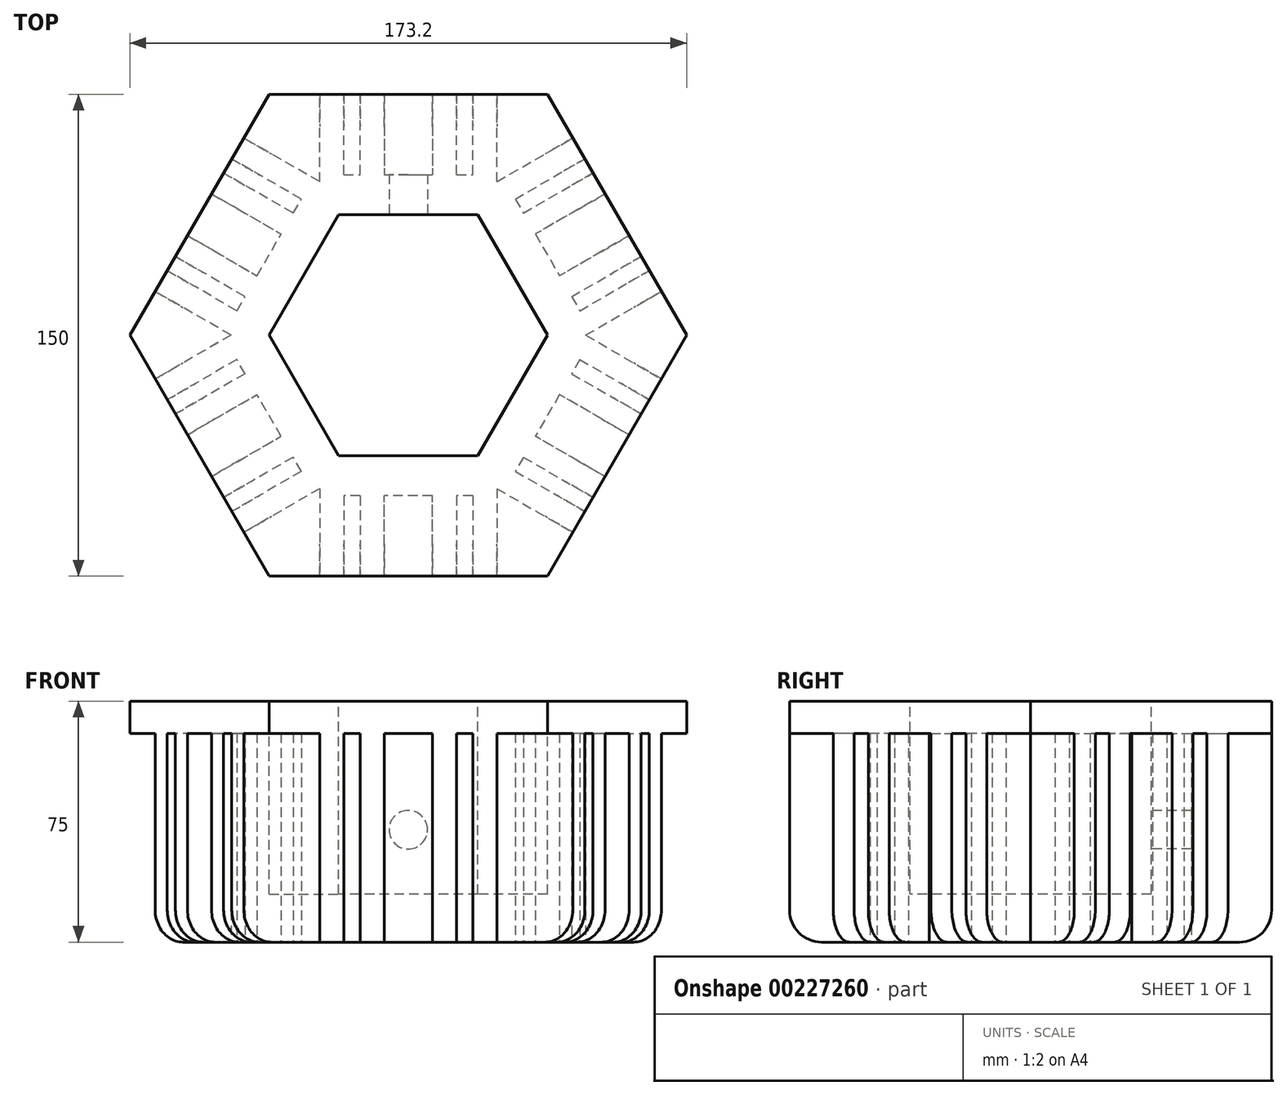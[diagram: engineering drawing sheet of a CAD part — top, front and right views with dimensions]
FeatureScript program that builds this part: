
annotation { "Feature Type Name" : "Feature", "Feature Type Description" : "" }
export const myFeature = defineFeature(function(context is Context, id is Id, definition is map)
    precondition{}
    {
        {
            var Q0;
            Q0=qCreatedBy(makeId("Top.planeOp"),FACE);
            var sketch = newSketch(context, id + "F0", { "sketchPlane" : qUnion([Q0])});
            skCircle(sketch, "E0.cCircle", {"center": v(0, 0) * mm, "radius": 75 * mm, "construction": true});
            skLineSegment(sketch, "E0.0", {"start": v(43.3, -75) * mm, "end": v(-43.3, -75) * mm});
            skLineSegment(sketch, "E0.1", {"start": v(-43.3, -75) * mm, "end": v(-86.6, 0) * mm});
            skLineSegment(sketch, "E0.2", {"start": v(-86.6, 0) * mm, "end": v(-43.3, 75) * mm});
            skLineSegment(sketch, "E0.3", {"start": v(-43.3, 75) * mm, "end": v(43.3, 75) * mm});
            skLineSegment(sketch, "E0.4", {"start": v(43.3, 75) * mm, "end": v(86.6, 0) * mm});
            skLineSegment(sketch, "E0.5", {"start": v(86.6, 0) * mm, "end": v(43.3, -75) * mm});
            skPoint(sketch, "E0.0.midPoint", {"position": v(0, -75) * mm});
            skCircle(sketch, "E1.cCircle", {"center": v(0, 0) * mm, "radius": 37.5 * mm, "construction": true});
            skLineSegment(sketch, "E1.0", {"start": v(21.65, -37.5) * mm, "end": v(-21.65, -37.5) * mm});
            skLineSegment(sketch, "E1.1", {"start": v(-21.65, -37.5) * mm, "end": v(-43.3, 0) * mm});
            skLineSegment(sketch, "E1.2", {"start": v(-43.3, 0) * mm, "end": v(-21.65, 37.5) * mm});
            skLineSegment(sketch, "E1.3", {"start": v(-21.65, 37.5) * mm, "end": v(21.65, 37.5) * mm});
            skLineSegment(sketch, "E1.4", {"start": v(21.65, 37.5) * mm, "end": v(43.3, 0) * mm});
            skLineSegment(sketch, "E1.5", {"start": v(43.3, 0) * mm, "end": v(21.65, -37.5) * mm});
            skPoint(sketch, "E1.0.midPoint", {"position": v(0, -37.5) * mm});
            skLineSegment(sketch, "E2", {"start": v(-15, 37.5) * mm, "end": v(-15, 75) * mm});
            skLineSegment(sketch, "E3", {"start": v(-20.08, 37.5) * mm, "end": v(-20.08, 75) * mm});
            skLineSegment(sketch, "E4", {"start": v(-27.58, 37.5) * mm, "end": v(-27.58, 75) * mm});
            skLineSegment(sketch, "E5", {"start": v(-7.5, 75) * mm, "end": v(-7.5, 37.5) * mm});
            skLineSegment(sketch, "E6.MirrorCS", {"start": v(7.5, 75) * mm, "end": v(7.5, 37.5) * mm});
            skLineSegment(sketch, "E7.MirrorCS", {"start": v(15, 37.5) * mm, "end": v(15, 75) * mm});
            skLineSegment(sketch, "E8.MirrorCS", {"start": v(20.08, 37.5) * mm, "end": v(20.08, 75) * mm});
            skLineSegment(sketch, "E9.MirrorCS", {"start": v(27.58, 37.5) * mm, "end": v(27.58, 75) * mm});
            skLineSegment(sketch, "E10", {"start": v(-27.58, 50) * mm, "end": v(27.58, 50) * mm});
            skLineSegment(sketch, "E11.1.0", {"start": v(-42.52, 1.36) * mm, "end": v(-75, 20.11) * mm});
            skLineSegment(sketch, "E11.1.1", {"start": v(-46.27, -5.13) * mm, "end": v(-78.74, 13.62) * mm});
            skLineSegment(sketch, "E11.1.2", {"start": v(-39.98, 5.76) * mm, "end": v(-72.45, 24.5) * mm});
            skLineSegment(sketch, "E11.1.3", {"start": v(-68.7, 31) * mm, "end": v(-36.23, 12.25) * mm});
            skLineSegment(sketch, "E11.1.4", {"start": v(-61.2, 44) * mm, "end": v(-28.73, 25.25) * mm});
            skLineSegment(sketch, "E11.1.5", {"start": v(-24.98, 31.74) * mm, "end": v(-57.45, 50.5) * mm});
            skLineSegment(sketch, "E11.1.6", {"start": v(-22.44, 36.14) * mm, "end": v(-54.91, 54.89) * mm});
            skLineSegment(sketch, "E11.1.7", {"start": v(-18.69, 42.63) * mm, "end": v(-51.16, 61.38) * mm});
            skLineSegment(sketch, "E11.1.8", {"start": v(-57.1, 1.12) * mm, "end": v(-29.51, 48.88) * mm});
            skLineSegment(sketch, "E11.2.0", {"start": v(-22.44, -36.14) * mm, "end": v(-54.91, -54.89) * mm});
            skLineSegment(sketch, "E11.2.1", {"start": v(-18.69, -42.63) * mm, "end": v(-51.16, -61.38) * mm});
            skLineSegment(sketch, "E11.2.2", {"start": v(-24.98, -31.74) * mm, "end": v(-57.45, -50.5) * mm});
            skLineSegment(sketch, "E11.2.3", {"start": v(-61.2, -44) * mm, "end": v(-28.73, -25.25) * mm});
            skLineSegment(sketch, "E11.2.4", {"start": v(-68.7, -31) * mm, "end": v(-36.23, -12.25) * mm});
            skLineSegment(sketch, "E11.2.5", {"start": v(-39.98, -5.76) * mm, "end": v(-72.45, -24.5) * mm});
            skLineSegment(sketch, "E11.2.6", {"start": v(-42.52, -1.36) * mm, "end": v(-75, -20.11) * mm});
            skLineSegment(sketch, "E11.2.7", {"start": v(-46.27, 5.13) * mm, "end": v(-78.74, -13.62) * mm});
            skLineSegment(sketch, "E11.2.8", {"start": v(-29.51, -48.88) * mm, "end": v(-57.1, -1.12) * mm});
            skLineSegment(sketch, "E11.3.0", {"start": v(20.08, -37.5) * mm, "end": v(20.08, -75) * mm});
            skLineSegment(sketch, "E11.3.1", {"start": v(27.58, -37.5) * mm, "end": v(27.58, -75) * mm});
            skLineSegment(sketch, "E11.3.2", {"start": v(15, -37.5) * mm, "end": v(15, -75) * mm});
            skLineSegment(sketch, "E11.3.3", {"start": v(7.5, -75) * mm, "end": v(7.5, -37.5) * mm});
            skLineSegment(sketch, "E11.3.4", {"start": v(-7.5, -75) * mm, "end": v(-7.5, -37.5) * mm});
            skLineSegment(sketch, "E11.3.5", {"start": v(-15, -37.5) * mm, "end": v(-15, -75) * mm});
            skLineSegment(sketch, "E11.3.6", {"start": v(-20.08, -37.5) * mm, "end": v(-20.08, -75) * mm});
            skLineSegment(sketch, "E11.3.7", {"start": v(-27.58, -37.5) * mm, "end": v(-27.58, -75) * mm});
            skLineSegment(sketch, "E11.3.8", {"start": v(27.58, -50) * mm, "end": v(-27.58, -50) * mm});
            skLineSegment(sketch, "E11.4.0", {"start": v(42.52, -1.36) * mm, "end": v(75, -20.11) * mm});
            skLineSegment(sketch, "E11.4.1", {"start": v(46.27, 5.13) * mm, "end": v(78.74, -13.62) * mm});
            skLineSegment(sketch, "E11.4.2", {"start": v(39.98, -5.76) * mm, "end": v(72.45, -24.5) * mm});
            skLineSegment(sketch, "E11.4.3", {"start": v(68.7, -31) * mm, "end": v(36.23, -12.25) * mm});
            skLineSegment(sketch, "E11.4.4", {"start": v(61.2, -44) * mm, "end": v(28.73, -25.25) * mm});
            skLineSegment(sketch, "E11.4.5", {"start": v(24.98, -31.74) * mm, "end": v(57.45, -50.5) * mm});
            skLineSegment(sketch, "E11.4.6", {"start": v(22.44, -36.14) * mm, "end": v(54.91, -54.89) * mm});
            skLineSegment(sketch, "E11.4.7", {"start": v(18.69, -42.63) * mm, "end": v(51.16, -61.38) * mm});
            skLineSegment(sketch, "E11.4.8", {"start": v(57.1, -1.12) * mm, "end": v(29.51, -48.88) * mm});
            skLineSegment(sketch, "E11.5.0", {"start": v(22.44, 36.14) * mm, "end": v(54.91, 54.89) * mm});
            skLineSegment(sketch, "E11.5.1", {"start": v(18.69, 42.63) * mm, "end": v(51.16, 61.38) * mm});
            skLineSegment(sketch, "E11.5.2", {"start": v(24.98, 31.74) * mm, "end": v(57.45, 50.5) * mm});
            skLineSegment(sketch, "E11.5.3", {"start": v(61.2, 44) * mm, "end": v(28.73, 25.25) * mm});
            skLineSegment(sketch, "E11.5.4", {"start": v(68.7, 31) * mm, "end": v(36.23, 12.25) * mm});
            skLineSegment(sketch, "E11.5.5", {"start": v(39.98, 5.76) * mm, "end": v(72.45, 24.5) * mm});
            skLineSegment(sketch, "E11.5.6", {"start": v(42.52, 1.36) * mm, "end": v(75, 20.11) * mm});
            skLineSegment(sketch, "E11.5.7", {"start": v(46.27, -5.13) * mm, "end": v(78.74, 13.62) * mm});
            skLineSegment(sketch, "E11.5.8", {"start": v(29.51, 48.88) * mm, "end": v(57.1, 1.12) * mm});
            skSolve(sketch);
        }
        {
            var Q0;
            {var subQ0=sQuery(id+"F0.wireOp",EDGE,"E3");var subQ1=sQuery(id+"F0.wireOp",EDGE,"E0.3");var subQ2=makeQuery(id+"F0.imprint","INTERSECT",VERTEX,{"derivedFrom":[subQ1,subQ0]});Q0=makeQuery(id+"F0.imprint","IMPRINT",FACE,{"disambiguationData":[TD([[makeQuery(id+"F0.imprint","IMPRINT",EDGE,{"disambiguationData":[TD([[subQ2,1.0]])],"derivedFrom":subQ1}),-1.0]])]});}
            var Q1;
            {var subQ0=sQuery(id+"F0.wireOp",EDGE,"E2");var subQ1=sQuery(id+"F0.wireOp",EDGE,"E0.3");var subQ2=makeQuery(id+"F0.imprint","INTERSECT",VERTEX,{"derivedFrom":[subQ1,subQ0]});Q1=makeQuery(id+"F0.imprint","IMPRINT",FACE,{"disambiguationData":[TD([[makeQuery(id+"F0.imprint","IMPRINT",EDGE,{"disambiguationData":[TD([[subQ2,1.0]])],"derivedFrom":subQ1}),-1.0]])]});}
            var Q2;
            {var subQ0=sQuery(id+"F0.wireOp",EDGE,"E2");var subQ1=sQuery(id+"F0.wireOp",EDGE,"E0.3");var subQ2=makeQuery(id+"F0.imprint","INTERSECT",VERTEX,{"derivedFrom":[subQ1,subQ0]});Q2=makeQuery(id+"F0.imprint","IMPRINT",FACE,{"disambiguationData":[TD([[makeQuery(id+"F0.imprint","IMPRINT",EDGE,{"disambiguationData":[TD([[subQ2,-1.0]])],"derivedFrom":subQ1}),-1.0]])]});}
            var Q3;
            {var subQ0=sQuery(id+"F0.wireOp",EDGE,"E5");var subQ1=sQuery(id+"F0.wireOp",EDGE,"E0.3");var subQ2=makeQuery(id+"F0.imprint","INTERSECT",VERTEX,{"derivedFrom":[subQ1,subQ0]});Q3=makeQuery(id+"F0.imprint","IMPRINT",FACE,{"disambiguationData":[TD([[makeQuery(id+"F0.imprint","IMPRINT",EDGE,{"disambiguationData":[TD([[subQ2,-1.0]])],"derivedFrom":subQ1}),-1.0]])]});}
            var Q4;
            {var subQ0=sQuery(id+"F0.wireOp",EDGE,"E6.MirrorCS");var subQ1=sQuery(id+"F0.wireOp",EDGE,"E0.3");var subQ2=makeQuery(id+"F0.imprint","INTERSECT",VERTEX,{"derivedFrom":[subQ1,subQ0]});Q4=makeQuery(id+"F0.imprint","IMPRINT",FACE,{"disambiguationData":[TD([[makeQuery(id+"F0.imprint","IMPRINT",EDGE,{"disambiguationData":[TD([[subQ2,-1.0]])],"derivedFrom":subQ1}),-1.0]])]});}
            var Q5;
            {var subQ0=sQuery(id+"F0.wireOp",EDGE,"E7.MirrorCS");var subQ1=sQuery(id+"F0.wireOp",EDGE,"E0.3");var subQ2=makeQuery(id+"F0.imprint","INTERSECT",VERTEX,{"derivedFrom":[subQ1,subQ0]});Q5=makeQuery(id+"F0.imprint","IMPRINT",FACE,{"disambiguationData":[TD([[makeQuery(id+"F0.imprint","IMPRINT",EDGE,{"disambiguationData":[TD([[subQ2,-1.0]])],"derivedFrom":subQ1}),-1.0]])]});}
            var Q6;
            {var subQ0=sQuery(id+"F0.wireOp",EDGE,"E8.MirrorCS");var subQ1=sQuery(id+"F0.wireOp",EDGE,"E0.3");var subQ2=makeQuery(id+"F0.imprint","INTERSECT",VERTEX,{"derivedFrom":[subQ1,subQ0]});Q6=makeQuery(id+"F0.imprint","IMPRINT",FACE,{"disambiguationData":[TD([[makeQuery(id+"F0.imprint","IMPRINT",EDGE,{"disambiguationData":[TD([[subQ2,-1.0]])],"derivedFrom":subQ1}),-1.0]])]});}
            var Q7;
            {var subQ1=sQuery(id+"F0.wireOp",EDGE,"E0.3");var subQ6=sQuery(id+"F0.wireOp",EDGE,"E0.4");var subQ7=makeQuery(id+"F0.imprint","INTERSECT",VERTEX,{"derivedFrom":[subQ1,subQ6]});Q7=makeQuery(id+"F0.imprint","IMPRINT",FACE,{"disambiguationData":[TD([[makeQuery(id+"F0.imprint","IMPRINT",EDGE,{"disambiguationData":[TD([[subQ7,1.0]])],"derivedFrom":subQ1}),-1.0]])]});}
            var Q8;
            {var subQ0=sQuery(id+"F0.wireOp",EDGE,"E11.5.0");var subQ1=sQuery(id+"F0.wireOp",EDGE,"E0.4");var subQ2=makeQuery(id+"F0.imprint","INTERSECT",VERTEX,{"derivedFrom":[subQ1,subQ0]});Q8=makeQuery(id+"F0.imprint","IMPRINT",FACE,{"disambiguationData":[TD([[makeQuery(id+"F0.imprint","IMPRINT",EDGE,{"disambiguationData":[TD([[subQ2,1.0]])],"derivedFrom":subQ1}),-1.0]])]});}
            var Q9;
            {var subQ0=sQuery(id+"F0.wireOp",EDGE,"E11.1.7");var subQ1=sQuery(id+"F0.wireOp",EDGE,"E3");var subQ2=makeQuery(id+"F0.imprint","INTERSECT",VERTEX,{"derivedFrom":[subQ1,subQ0]});Q9=makeQuery(id+"F0.imprint","IMPRINT",FACE,{"disambiguationData":[TD([[makeQuery(id+"F0.imprint","IMPRINT",EDGE,{"disambiguationData":[TD([[subQ2,-1.0]])],"derivedFrom":subQ1}),1.0]])]});}
            var Q10;
            {var subQ6=sQuery(id+"F0.wireOp",EDGE,"E1.3");var subQ9=sQuery(id+"F0.wireOp",EDGE,"E1.2");var subQ10=makeQuery(id+"F0.imprint","INTERSECT",VERTEX,{"derivedFrom":[subQ9,subQ6]});Q10=makeQuery(id+"F0.imprint","IMPRINT",FACE,{"disambiguationData":[TD([[makeQuery(id+"F0.imprint","IMPRINT",EDGE,{"disambiguationData":[TD([[subQ10,1.0]])],"derivedFrom":subQ9}),1.0]])]});}
            var Q11;
            {var subQ4=sQuery(id+"F0.wireOp",EDGE,"E1.3");var subQ6=sQuery(id+"F0.wireOp",EDGE,"E2");var subQ7=makeQuery(id+"F0.imprint","INTERSECT",VERTEX,{"derivedFrom":[subQ4,subQ6]});Q11=makeQuery(id+"F0.imprint","IMPRINT",FACE,{"disambiguationData":[TD([[makeQuery(id+"F0.imprint","IMPRINT",EDGE,{"disambiguationData":[TD([[subQ7,1.0]])],"derivedFrom":subQ4}),1.0]])]});}
            var Q12;
            {var subQ0=sQuery(id+"F0.wireOp",EDGE,"E2");var subQ1=sQuery(id+"F0.wireOp",EDGE,"E1.3");var subQ2=makeQuery(id+"F0.imprint","INTERSECT",VERTEX,{"derivedFrom":[subQ1,subQ0]});Q12=makeQuery(id+"F0.imprint","IMPRINT",FACE,{"disambiguationData":[TD([[makeQuery(id+"F0.imprint","IMPRINT",EDGE,{"disambiguationData":[TD([[subQ2,-1.0]])],"derivedFrom":subQ1}),1.0]])]});}
            var Q13;
            {var subQ0=sQuery(id+"F0.wireOp",EDGE,"E5");var subQ1=sQuery(id+"F0.wireOp",EDGE,"E1.3");var subQ2=makeQuery(id+"F0.imprint","INTERSECT",VERTEX,{"derivedFrom":[subQ1,subQ0]});Q13=makeQuery(id+"F0.imprint","IMPRINT",FACE,{"disambiguationData":[TD([[makeQuery(id+"F0.imprint","IMPRINT",EDGE,{"disambiguationData":[TD([[subQ2,-1.0]])],"derivedFrom":subQ1}),1.0]])]});}
            var Q14;
            {var subQ0=sQuery(id+"F0.wireOp",EDGE,"E6.MirrorCS");var subQ1=sQuery(id+"F0.wireOp",EDGE,"E1.3");var subQ2=makeQuery(id+"F0.imprint","INTERSECT",VERTEX,{"derivedFrom":[subQ1,subQ0]});Q14=makeQuery(id+"F0.imprint","IMPRINT",FACE,{"disambiguationData":[TD([[makeQuery(id+"F0.imprint","IMPRINT",EDGE,{"disambiguationData":[TD([[subQ2,-1.0]])],"derivedFrom":subQ1}),1.0]])]});}
            var Q15;
            {var subQ4=sQuery(id+"F0.wireOp",EDGE,"E1.3");var subQ6=sQuery(id+"F0.wireOp",EDGE,"E7.MirrorCS");var subQ8=makeQuery(id+"F0.imprint","INTERSECT",VERTEX,{"derivedFrom":[subQ4,subQ6]});Q15=makeQuery(id+"F0.imprint","IMPRINT",FACE,{"disambiguationData":[TD([[makeQuery(id+"F0.imprint","IMPRINT",EDGE,{"disambiguationData":[TD([[subQ8,-1.0]])],"derivedFrom":subQ4}),1.0]])]});}
            var Q16;
            {var subQ5=sQuery(id+"F0.wireOp",EDGE,"E1.4");var subQ6=sQuery(id+"F0.wireOp",EDGE,"E1.3");var subQ7=makeQuery(id+"F0.imprint","INTERSECT",VERTEX,{"derivedFrom":[subQ6,subQ5]});Q16=makeQuery(id+"F0.imprint","IMPRINT",FACE,{"disambiguationData":[TD([[makeQuery(id+"F0.imprint","IMPRINT",EDGE,{"disambiguationData":[TD([[subQ7,1.0]])],"derivedFrom":subQ6}),1.0]])]});}
            var Q17;
            {var subQ0=sQuery(id+"F0.wireOp",EDGE,"E11.5.1");var subQ1=sQuery(id+"F0.wireOp",EDGE,"E8.MirrorCS");var subQ2=makeQuery(id+"F0.imprint","INTERSECT",VERTEX,{"derivedFrom":[subQ1,subQ0]});Q17=makeQuery(id+"F0.imprint","IMPRINT",FACE,{"disambiguationData":[TD([[makeQuery(id+"F0.imprint","IMPRINT",EDGE,{"disambiguationData":[TD([[subQ2,-1.0]])],"derivedFrom":subQ1}),-1.0]])]});}
            var Q18;
            {var subQ0=sQuery(id+"F0.wireOp",EDGE,"E11.5.0");var subQ1=sQuery(id+"F0.wireOp",EDGE,"E9.MirrorCS");var subQ2=makeQuery(id+"F0.imprint","INTERSECT",VERTEX,{"derivedFrom":[subQ1,subQ0]});Q18=makeQuery(id+"F0.imprint","IMPRINT",FACE,{"disambiguationData":[TD([[makeQuery(id+"F0.imprint","IMPRINT",EDGE,{"disambiguationData":[TD([[subQ2,-1.0]])],"derivedFrom":subQ1}),-1.0]])]});}
            var Q19;
            {var subQ1=sQuery(id+"F0.wireOp",EDGE,"E1.4");var subQ5=sQuery(id+"F0.wireOp",EDGE,"E11.5.0");var subQ8=makeQuery(id+"F0.imprint","INTERSECT",VERTEX,{"derivedFrom":[subQ1,subQ5]});Q19=makeQuery(id+"F0.imprint","IMPRINT",FACE,{"disambiguationData":[TD([[makeQuery(id+"F0.imprint","IMPRINT",EDGE,{"disambiguationData":[TD([[subQ8,-1.0]])],"derivedFrom":subQ1}),1.0]])]});}
            var Q20;
            {var subQ0=sQuery(id+"F0.wireOp",EDGE,"E11.5.0");var subQ1=sQuery(id+"F0.wireOp",EDGE,"E0.4");var subQ2=makeQuery(id+"F0.imprint","INTERSECT",VERTEX,{"derivedFrom":[subQ1,subQ0]});Q20=makeQuery(id+"F0.imprint","IMPRINT",FACE,{"disambiguationData":[TD([[makeQuery(id+"F0.imprint","IMPRINT",EDGE,{"disambiguationData":[TD([[subQ2,-1.0]])],"derivedFrom":subQ1}),-1.0]])]});}
            var Q21;
            {var subQ0=sQuery(id+"F0.wireOp",EDGE,"E11.5.2");var subQ1=sQuery(id+"F0.wireOp",EDGE,"E1.4");var subQ2=makeQuery(id+"F0.imprint","INTERSECT",VERTEX,{"derivedFrom":[subQ1,subQ0]});Q21=makeQuery(id+"F0.imprint","IMPRINT",FACE,{"disambiguationData":[TD([[makeQuery(id+"F0.imprint","IMPRINT",EDGE,{"disambiguationData":[TD([[subQ2,-1.0]])],"derivedFrom":subQ1}),1.0]])]});}
            var Q22;
            {var subQ0=sQuery(id+"F0.wireOp",EDGE,"E11.5.2");var subQ1=sQuery(id+"F0.wireOp",EDGE,"E0.4");var subQ2=makeQuery(id+"F0.imprint","INTERSECT",VERTEX,{"derivedFrom":[subQ1,subQ0]});Q22=makeQuery(id+"F0.imprint","IMPRINT",FACE,{"disambiguationData":[TD([[makeQuery(id+"F0.imprint","IMPRINT",EDGE,{"disambiguationData":[TD([[subQ2,-1.0]])],"derivedFrom":subQ1}),-1.0]])]});}
            var Q23;
            {var subQ0=sQuery(id+"F0.wireOp",EDGE,"E11.5.3");var subQ1=sQuery(id+"F0.wireOp",EDGE,"E1.4");var subQ2=makeQuery(id+"F0.imprint","INTERSECT",VERTEX,{"derivedFrom":[subQ1,subQ0]});Q23=makeQuery(id+"F0.imprint","IMPRINT",FACE,{"disambiguationData":[TD([[makeQuery(id+"F0.imprint","IMPRINT",EDGE,{"disambiguationData":[TD([[subQ2,-1.0]])],"derivedFrom":subQ1}),1.0]])]});}
            var Q24;
            {var subQ0=sQuery(id+"F0.wireOp",EDGE,"E11.5.3");var subQ1=sQuery(id+"F0.wireOp",EDGE,"E0.4");var subQ2=makeQuery(id+"F0.imprint","INTERSECT",VERTEX,{"derivedFrom":[subQ1,subQ0]});Q24=makeQuery(id+"F0.imprint","IMPRINT",FACE,{"disambiguationData":[TD([[makeQuery(id+"F0.imprint","IMPRINT",EDGE,{"disambiguationData":[TD([[subQ2,-1.0]])],"derivedFrom":subQ1}),-1.0]])]});}
            var Q25;
            {var subQ0=sQuery(id+"F0.wireOp",EDGE,"E11.5.4");var subQ1=sQuery(id+"F0.wireOp",EDGE,"E1.4");var subQ2=makeQuery(id+"F0.imprint","INTERSECT",VERTEX,{"derivedFrom":[subQ1,subQ0]});Q25=makeQuery(id+"F0.imprint","IMPRINT",FACE,{"disambiguationData":[TD([[makeQuery(id+"F0.imprint","IMPRINT",EDGE,{"disambiguationData":[TD([[subQ2,-1.0]])],"derivedFrom":subQ1}),1.0]])]});}
            var Q26;
            {var subQ0=sQuery(id+"F0.wireOp",EDGE,"E11.5.4");var subQ1=sQuery(id+"F0.wireOp",EDGE,"E0.4");var subQ2=makeQuery(id+"F0.imprint","INTERSECT",VERTEX,{"derivedFrom":[subQ1,subQ0]});Q26=makeQuery(id+"F0.imprint","IMPRINT",FACE,{"disambiguationData":[TD([[makeQuery(id+"F0.imprint","IMPRINT",EDGE,{"disambiguationData":[TD([[subQ2,-1.0]])],"derivedFrom":subQ1}),-1.0]])]});}
            var Q27;
            {var subQ4=sQuery(id+"F0.wireOp",EDGE,"E1.4");var subQ6=sQuery(id+"F0.wireOp",EDGE,"E11.5.5");var subQ8=makeQuery(id+"F0.imprint","INTERSECT",VERTEX,{"derivedFrom":[subQ4,subQ6]});Q27=makeQuery(id+"F0.imprint","IMPRINT",FACE,{"disambiguationData":[TD([[makeQuery(id+"F0.imprint","IMPRINT",EDGE,{"disambiguationData":[TD([[subQ8,-1.0]])],"derivedFrom":subQ4}),1.0]])]});}
            var Q28;
            {var subQ6=sQuery(id+"F0.wireOp",EDGE,"E1.5");var subQ9=sQuery(id+"F0.wireOp",EDGE,"E1.4");var subQ10=makeQuery(id+"F0.imprint","INTERSECT",VERTEX,{"derivedFrom":[subQ9,subQ6]});Q28=makeQuery(id+"F0.imprint","IMPRINT",FACE,{"disambiguationData":[TD([[makeQuery(id+"F0.imprint","IMPRINT",EDGE,{"disambiguationData":[TD([[subQ10,1.0]])],"derivedFrom":subQ9}),1.0]])]});}
            var Q29;
            {var subQ0=sQuery(id+"F0.wireOp",EDGE,"E11.5.6");var subQ1=sQuery(id+"F0.wireOp",EDGE,"E11.4.1");var subQ2=makeQuery(id+"F0.imprint","INTERSECT",VERTEX,{"derivedFrom":[subQ1,subQ0]});Q29=makeQuery(id+"F0.imprint","IMPRINT",FACE,{"disambiguationData":[TD([[makeQuery(id+"F0.imprint","IMPRINT",EDGE,{"disambiguationData":[TD([[subQ2,-1.0]])],"derivedFrom":subQ1}),1.0]])]});}
            var Q30;
            {var subQ0=sQuery(id+"F0.wireOp",EDGE,"E11.5.5");var subQ1=sQuery(id+"F0.wireOp",EDGE,"E0.4");var subQ2=makeQuery(id+"F0.imprint","INTERSECT",VERTEX,{"derivedFrom":[subQ1,subQ0]});Q30=makeQuery(id+"F0.imprint","IMPRINT",FACE,{"disambiguationData":[TD([[makeQuery(id+"F0.imprint","IMPRINT",EDGE,{"disambiguationData":[TD([[subQ2,-1.0]])],"derivedFrom":subQ1}),-1.0]])]});}
            var Q31;
            {var subQ0=sQuery(id+"F0.wireOp",EDGE,"E11.5.6");var subQ1=sQuery(id+"F0.wireOp",EDGE,"E0.4");var subQ2=makeQuery(id+"F0.imprint","INTERSECT",VERTEX,{"derivedFrom":[subQ1,subQ0]});Q31=makeQuery(id+"F0.imprint","IMPRINT",FACE,{"disambiguationData":[TD([[makeQuery(id+"F0.imprint","IMPRINT",EDGE,{"disambiguationData":[TD([[subQ2,-1.0]])],"derivedFrom":subQ1}),-1.0]])]});}
            var Q32;
            {var subQ1=sQuery(id+"F0.wireOp",EDGE,"E0.5");var subQ6=sQuery(id+"F0.wireOp",EDGE,"E0.4");var subQ7=makeQuery(id+"F0.imprint","INTERSECT",VERTEX,{"derivedFrom":[subQ6,subQ1]});Q32=makeQuery(id+"F0.imprint","IMPRINT",FACE,{"disambiguationData":[TD([[makeQuery(id+"F0.imprint","IMPRINT",EDGE,{"disambiguationData":[TD([[subQ7,1.0]])],"derivedFrom":subQ6}),-1.0]])]});}
            var Q33;
            {var subQ0=sQuery(id+"F0.wireOp",EDGE,"E11.4.0");var subQ1=sQuery(id+"F0.wireOp",EDGE,"E0.5");var subQ2=makeQuery(id+"F0.imprint","INTERSECT",VERTEX,{"derivedFrom":[subQ1,subQ0]});Q33=makeQuery(id+"F0.imprint","IMPRINT",FACE,{"disambiguationData":[TD([[makeQuery(id+"F0.imprint","IMPRINT",EDGE,{"disambiguationData":[TD([[subQ2,1.0]])],"derivedFrom":subQ1}),-1.0]])]});}
            var Q34;
            {var subQ0=sQuery(id+"F0.wireOp",EDGE,"E11.5.7");var subQ1=sQuery(id+"F0.wireOp",EDGE,"E11.4.0");var subQ2=makeQuery(id+"F0.imprint","INTERSECT",VERTEX,{"derivedFrom":[subQ1,subQ0]});Q34=makeQuery(id+"F0.imprint","IMPRINT",FACE,{"disambiguationData":[TD([[makeQuery(id+"F0.imprint","IMPRINT",EDGE,{"disambiguationData":[TD([[subQ2,-1.0]])],"derivedFrom":subQ1}),1.0]])]});}
            var Q35;
            {var subQ1=sQuery(id+"F0.wireOp",EDGE,"E1.5");var subQ5=sQuery(id+"F0.wireOp",EDGE,"E11.4.0");var subQ6=makeQuery(id+"F0.imprint","INTERSECT",VERTEX,{"derivedFrom":[subQ1,subQ5]});Q35=makeQuery(id+"F0.imprint","IMPRINT",FACE,{"disambiguationData":[TD([[makeQuery(id+"F0.imprint","IMPRINT",EDGE,{"disambiguationData":[TD([[subQ6,-1.0]])],"derivedFrom":subQ1}),1.0]])]});}
            var Q36;
            {var subQ0=sQuery(id+"F0.wireOp",EDGE,"E11.4.0");var subQ1=sQuery(id+"F0.wireOp",EDGE,"E0.5");var subQ2=makeQuery(id+"F0.imprint","INTERSECT",VERTEX,{"derivedFrom":[subQ1,subQ0]});Q36=makeQuery(id+"F0.imprint","IMPRINT",FACE,{"disambiguationData":[TD([[makeQuery(id+"F0.imprint","IMPRINT",EDGE,{"disambiguationData":[TD([[subQ2,-1.0]])],"derivedFrom":subQ1}),-1.0]])]});}
            var Q37;
            {var subQ0=sQuery(id+"F0.wireOp",EDGE,"E11.4.2");var subQ1=sQuery(id+"F0.wireOp",EDGE,"E0.5");var subQ2=makeQuery(id+"F0.imprint","INTERSECT",VERTEX,{"derivedFrom":[subQ1,subQ0]});Q37=makeQuery(id+"F0.imprint","IMPRINT",FACE,{"disambiguationData":[TD([[makeQuery(id+"F0.imprint","IMPRINT",EDGE,{"disambiguationData":[TD([[subQ2,-1.0]])],"derivedFrom":subQ1}),-1.0]])]});}
            var Q38;
            {var subQ0=sQuery(id+"F0.wireOp",EDGE,"E11.4.2");var subQ1=sQuery(id+"F0.wireOp",EDGE,"E1.5");var subQ2=makeQuery(id+"F0.imprint","INTERSECT",VERTEX,{"derivedFrom":[subQ1,subQ0]});Q38=makeQuery(id+"F0.imprint","IMPRINT",FACE,{"disambiguationData":[TD([[makeQuery(id+"F0.imprint","IMPRINT",EDGE,{"disambiguationData":[TD([[subQ2,-1.0]])],"derivedFrom":subQ1}),1.0]])]});}
            var Q39;
            {var subQ0=sQuery(id+"F0.wireOp",EDGE,"E11.4.3");var subQ1=sQuery(id+"F0.wireOp",EDGE,"E1.5");var subQ2=makeQuery(id+"F0.imprint","INTERSECT",VERTEX,{"derivedFrom":[subQ1,subQ0]});Q39=makeQuery(id+"F0.imprint","IMPRINT",FACE,{"disambiguationData":[TD([[makeQuery(id+"F0.imprint","IMPRINT",EDGE,{"disambiguationData":[TD([[subQ2,-1.0]])],"derivedFrom":subQ1}),1.0]])]});}
            var Q40;
            {var subQ0=sQuery(id+"F0.wireOp",EDGE,"E11.4.3");var subQ1=sQuery(id+"F0.wireOp",EDGE,"E0.5");var subQ2=makeQuery(id+"F0.imprint","INTERSECT",VERTEX,{"derivedFrom":[subQ1,subQ0]});Q40=makeQuery(id+"F0.imprint","IMPRINT",FACE,{"disambiguationData":[TD([[makeQuery(id+"F0.imprint","IMPRINT",EDGE,{"disambiguationData":[TD([[subQ2,-1.0]])],"derivedFrom":subQ1}),-1.0]])]});}
            var Q41;
            {var subQ0=sQuery(id+"F0.wireOp",EDGE,"E11.4.4");var subQ1=sQuery(id+"F0.wireOp",EDGE,"E1.5");var subQ2=makeQuery(id+"F0.imprint","INTERSECT",VERTEX,{"derivedFrom":[subQ1,subQ0]});Q41=makeQuery(id+"F0.imprint","IMPRINT",FACE,{"disambiguationData":[TD([[makeQuery(id+"F0.imprint","IMPRINT",EDGE,{"disambiguationData":[TD([[subQ2,-1.0]])],"derivedFrom":subQ1}),1.0]])]});}
            var Q42;
            {var subQ0=sQuery(id+"F0.wireOp",EDGE,"E11.4.4");var subQ1=sQuery(id+"F0.wireOp",EDGE,"E0.5");var subQ2=makeQuery(id+"F0.imprint","INTERSECT",VERTEX,{"derivedFrom":[subQ1,subQ0]});Q42=makeQuery(id+"F0.imprint","IMPRINT",FACE,{"disambiguationData":[TD([[makeQuery(id+"F0.imprint","IMPRINT",EDGE,{"disambiguationData":[TD([[subQ2,-1.0]])],"derivedFrom":subQ1}),-1.0]])]});}
            var Q43;
            {var subQ1=sQuery(id+"F0.wireOp",EDGE,"E1.5");var subQ6=sQuery(id+"F0.wireOp",EDGE,"E11.4.5");var subQ7=makeQuery(id+"F0.imprint","INTERSECT",VERTEX,{"derivedFrom":[subQ1,subQ6]});Q43=makeQuery(id+"F0.imprint","IMPRINT",FACE,{"disambiguationData":[TD([[makeQuery(id+"F0.imprint","IMPRINT",EDGE,{"disambiguationData":[TD([[subQ7,-1.0]])],"derivedFrom":subQ1}),1.0]])]});}
            var Q44;
            {var subQ0=sQuery(id+"F0.wireOp",EDGE,"E11.4.5");var subQ1=sQuery(id+"F0.wireOp",EDGE,"E0.5");var subQ2=makeQuery(id+"F0.imprint","INTERSECT",VERTEX,{"derivedFrom":[subQ1,subQ0]});Q44=makeQuery(id+"F0.imprint","IMPRINT",FACE,{"disambiguationData":[TD([[makeQuery(id+"F0.imprint","IMPRINT",EDGE,{"disambiguationData":[TD([[subQ2,-1.0]])],"derivedFrom":subQ1}),-1.0]])]});}
            var Q45;
            {var subQ0=sQuery(id+"F0.wireOp",EDGE,"E11.4.6");var subQ1=sQuery(id+"F0.wireOp",EDGE,"E0.5");var subQ2=makeQuery(id+"F0.imprint","INTERSECT",VERTEX,{"derivedFrom":[subQ1,subQ0]});Q45=makeQuery(id+"F0.imprint","IMPRINT",FACE,{"disambiguationData":[TD([[makeQuery(id+"F0.imprint","IMPRINT",EDGE,{"disambiguationData":[TD([[subQ2,-1.0]])],"derivedFrom":subQ1}),-1.0]])]});}
            var Q46;
            {var subQ6=sQuery(id+"F0.wireOp",EDGE,"E1.0");var subQ9=sQuery(id+"F0.wireOp",EDGE,"E1.5");var subQ10=makeQuery(id+"F0.imprint","INTERSECT",VERTEX,{"derivedFrom":[subQ6,subQ9]});Q46=makeQuery(id+"F0.imprint","IMPRINT",FACE,{"disambiguationData":[TD([[makeQuery(id+"F0.imprint","IMPRINT",EDGE,{"disambiguationData":[TD([[subQ10,-1.0]])],"derivedFrom":subQ6}),1.0]])]});}
            var Q47;
            {var subQ0=sQuery(id+"F0.wireOp",EDGE,"E11.4.6");var subQ1=sQuery(id+"F0.wireOp",EDGE,"E11.3.1");var subQ2=makeQuery(id+"F0.imprint","INTERSECT",VERTEX,{"derivedFrom":[subQ1,subQ0]});Q47=makeQuery(id+"F0.imprint","IMPRINT",FACE,{"disambiguationData":[TD([[makeQuery(id+"F0.imprint","IMPRINT",EDGE,{"disambiguationData":[TD([[subQ2,-1.0]])],"derivedFrom":subQ1}),1.0]])]});}
            var Q48;
            {var subQ1=sQuery(id+"F0.wireOp",EDGE,"E0.0");var subQ6=sQuery(id+"F0.wireOp",EDGE,"E0.5");var subQ7=makeQuery(id+"F0.imprint","INTERSECT",VERTEX,{"derivedFrom":[subQ1,subQ6]});Q48=makeQuery(id+"F0.imprint","IMPRINT",FACE,{"disambiguationData":[TD([[makeQuery(id+"F0.imprint","IMPRINT",EDGE,{"disambiguationData":[TD([[subQ7,-1.0]])],"derivedFrom":subQ1}),-1.0]])]});}
            var Q49;
            {var subQ0=sQuery(id+"F0.wireOp",EDGE,"E11.3.0");var subQ1=sQuery(id+"F0.wireOp",EDGE,"E0.0");var subQ2=makeQuery(id+"F0.imprint","INTERSECT",VERTEX,{"derivedFrom":[subQ1,subQ0]});Q49=makeQuery(id+"F0.imprint","IMPRINT",FACE,{"disambiguationData":[TD([[makeQuery(id+"F0.imprint","IMPRINT",EDGE,{"disambiguationData":[TD([[subQ2,1.0]])],"derivedFrom":subQ1}),-1.0]])]});}
            var Q50;
            {var subQ0=sQuery(id+"F0.wireOp",EDGE,"E11.4.7");var subQ1=sQuery(id+"F0.wireOp",EDGE,"E11.3.0");var subQ2=makeQuery(id+"F0.imprint","INTERSECT",VERTEX,{"derivedFrom":[subQ1,subQ0]});Q50=makeQuery(id+"F0.imprint","IMPRINT",FACE,{"disambiguationData":[TD([[makeQuery(id+"F0.imprint","IMPRINT",EDGE,{"disambiguationData":[TD([[subQ2,-1.0]])],"derivedFrom":subQ1}),1.0]])]});}
            var Q51;
            {var subQ1=sQuery(id+"F0.wireOp",EDGE,"E1.0");var subQ5=sQuery(id+"F0.wireOp",EDGE,"E11.3.0");var subQ8=makeQuery(id+"F0.imprint","INTERSECT",VERTEX,{"derivedFrom":[subQ1,subQ5]});Q51=makeQuery(id+"F0.imprint","IMPRINT",FACE,{"disambiguationData":[TD([[makeQuery(id+"F0.imprint","IMPRINT",EDGE,{"disambiguationData":[TD([[subQ8,-1.0]])],"derivedFrom":subQ1}),1.0]])]});}
            var Q52;
            {var subQ0=sQuery(id+"F0.wireOp",EDGE,"E11.3.0");var subQ1=sQuery(id+"F0.wireOp",EDGE,"E0.0");var subQ2=makeQuery(id+"F0.imprint","INTERSECT",VERTEX,{"derivedFrom":[subQ1,subQ0]});Q52=makeQuery(id+"F0.imprint","IMPRINT",FACE,{"disambiguationData":[TD([[makeQuery(id+"F0.imprint","IMPRINT",EDGE,{"disambiguationData":[TD([[subQ2,-1.0]])],"derivedFrom":subQ1}),-1.0]])]});}
            var Q53;
            {var subQ0=sQuery(id+"F0.wireOp",EDGE,"E11.3.2");var subQ1=sQuery(id+"F0.wireOp",EDGE,"E0.0");var subQ2=makeQuery(id+"F0.imprint","INTERSECT",VERTEX,{"derivedFrom":[subQ1,subQ0]});Q53=makeQuery(id+"F0.imprint","IMPRINT",FACE,{"disambiguationData":[TD([[makeQuery(id+"F0.imprint","IMPRINT",EDGE,{"disambiguationData":[TD([[subQ2,-1.0]])],"derivedFrom":subQ1}),-1.0]])]});}
            var Q54;
            {var subQ0=sQuery(id+"F0.wireOp",EDGE,"E11.3.2");var subQ1=sQuery(id+"F0.wireOp",EDGE,"E1.0");var subQ2=makeQuery(id+"F0.imprint","INTERSECT",VERTEX,{"derivedFrom":[subQ1,subQ0]});Q54=makeQuery(id+"F0.imprint","IMPRINT",FACE,{"disambiguationData":[TD([[makeQuery(id+"F0.imprint","IMPRINT",EDGE,{"disambiguationData":[TD([[subQ2,-1.0]])],"derivedFrom":subQ1}),1.0]])]});}
            var Q55;
            {var subQ0=sQuery(id+"F0.wireOp",EDGE,"E11.3.3");var subQ1=sQuery(id+"F0.wireOp",EDGE,"E1.0");var subQ2=makeQuery(id+"F0.imprint","INTERSECT",VERTEX,{"derivedFrom":[subQ1,subQ0]});Q55=makeQuery(id+"F0.imprint","IMPRINT",FACE,{"disambiguationData":[TD([[makeQuery(id+"F0.imprint","IMPRINT",EDGE,{"disambiguationData":[TD([[subQ2,-1.0]])],"derivedFrom":subQ1}),1.0]])]});}
            var Q56;
            {var subQ0=sQuery(id+"F0.wireOp",EDGE,"E11.3.3");var subQ1=sQuery(id+"F0.wireOp",EDGE,"E0.0");var subQ2=makeQuery(id+"F0.imprint","INTERSECT",VERTEX,{"derivedFrom":[subQ1,subQ0]});Q56=makeQuery(id+"F0.imprint","IMPRINT",FACE,{"disambiguationData":[TD([[makeQuery(id+"F0.imprint","IMPRINT",EDGE,{"disambiguationData":[TD([[subQ2,-1.0]])],"derivedFrom":subQ1}),-1.0]])]});}
            var Q57;
            {var subQ0=sQuery(id+"F0.wireOp",EDGE,"E11.3.4");var subQ1=sQuery(id+"F0.wireOp",EDGE,"E0.0");var subQ2=makeQuery(id+"F0.imprint","INTERSECT",VERTEX,{"derivedFrom":[subQ1,subQ0]});Q57=makeQuery(id+"F0.imprint","IMPRINT",FACE,{"disambiguationData":[TD([[makeQuery(id+"F0.imprint","IMPRINT",EDGE,{"disambiguationData":[TD([[subQ2,-1.0]])],"derivedFrom":subQ1}),-1.0]])]});}
            var Q58;
            {var subQ0=sQuery(id+"F0.wireOp",EDGE,"E11.3.4");var subQ1=sQuery(id+"F0.wireOp",EDGE,"E1.0");var subQ2=makeQuery(id+"F0.imprint","INTERSECT",VERTEX,{"derivedFrom":[subQ1,subQ0]});Q58=makeQuery(id+"F0.imprint","IMPRINT",FACE,{"disambiguationData":[TD([[makeQuery(id+"F0.imprint","IMPRINT",EDGE,{"disambiguationData":[TD([[subQ2,-1.0]])],"derivedFrom":subQ1}),1.0]])]});}
            var Q59;
            {var subQ0=sQuery(id+"F0.wireOp",EDGE,"E11.3.5");var subQ1=sQuery(id+"F0.wireOp",EDGE,"E0.0");var subQ2=makeQuery(id+"F0.imprint","INTERSECT",VERTEX,{"derivedFrom":[subQ1,subQ0]});Q59=makeQuery(id+"F0.imprint","IMPRINT",FACE,{"disambiguationData":[TD([[makeQuery(id+"F0.imprint","IMPRINT",EDGE,{"disambiguationData":[TD([[subQ2,-1.0]])],"derivedFrom":subQ1}),-1.0]])]});}
            var Q60;
            {var subQ4=sQuery(id+"F0.wireOp",EDGE,"E1.0");var subQ6=sQuery(id+"F0.wireOp",EDGE,"E11.3.5");var subQ7=makeQuery(id+"F0.imprint","INTERSECT",VERTEX,{"derivedFrom":[subQ4,subQ6]});Q60=makeQuery(id+"F0.imprint","IMPRINT",FACE,{"disambiguationData":[TD([[makeQuery(id+"F0.imprint","IMPRINT",EDGE,{"disambiguationData":[TD([[subQ7,-1.0]])],"derivedFrom":subQ4}),1.0]])]});}
            var Q61;
            {var subQ1=sQuery(id+"F0.wireOp",EDGE,"E1.1");var subQ5=sQuery(id+"F0.wireOp",EDGE,"E1.0");var subQ6=makeQuery(id+"F0.imprint","INTERSECT",VERTEX,{"derivedFrom":[subQ5,subQ1]});Q61=makeQuery(id+"F0.imprint","IMPRINT",FACE,{"disambiguationData":[TD([[makeQuery(id+"F0.imprint","IMPRINT",EDGE,{"disambiguationData":[TD([[subQ6,1.0]])],"derivedFrom":subQ5}),1.0]])]});}
            var Q62;
            {var subQ0=sQuery(id+"F0.wireOp",EDGE,"E11.3.6");var subQ1=sQuery(id+"F0.wireOp",EDGE,"E11.2.1");var subQ2=makeQuery(id+"F0.imprint","INTERSECT",VERTEX,{"derivedFrom":[subQ1,subQ0]});Q62=makeQuery(id+"F0.imprint","IMPRINT",FACE,{"disambiguationData":[TD([[makeQuery(id+"F0.imprint","IMPRINT",EDGE,{"disambiguationData":[TD([[subQ2,-1.0]])],"derivedFrom":subQ1}),1.0]])]});}
            var Q63;
            {var subQ0=sQuery(id+"F0.wireOp",EDGE,"E11.3.6");var subQ1=sQuery(id+"F0.wireOp",EDGE,"E0.0");var subQ2=makeQuery(id+"F0.imprint","INTERSECT",VERTEX,{"derivedFrom":[subQ1,subQ0]});Q63=makeQuery(id+"F0.imprint","IMPRINT",FACE,{"disambiguationData":[TD([[makeQuery(id+"F0.imprint","IMPRINT",EDGE,{"disambiguationData":[TD([[subQ2,-1.0]])],"derivedFrom":subQ1}),-1.0]])]});}
            var Q64;
            {var subQ4=sQuery(id+"F0.wireOp",EDGE,"E0.1");var subQ6=sQuery(id+"F0.wireOp",EDGE,"E0.0");var subQ7=makeQuery(id+"F0.imprint","INTERSECT",VERTEX,{"derivedFrom":[subQ6,subQ4]});Q64=makeQuery(id+"F0.imprint","IMPRINT",FACE,{"disambiguationData":[TD([[makeQuery(id+"F0.imprint","IMPRINT",EDGE,{"disambiguationData":[TD([[subQ7,1.0]])],"derivedFrom":subQ6}),-1.0]])]});}
            var Q65;
            {var subQ0=sQuery(id+"F0.wireOp",EDGE,"E11.3.7");var subQ1=sQuery(id+"F0.wireOp",EDGE,"E11.2.0");var subQ2=makeQuery(id+"F0.imprint","INTERSECT",VERTEX,{"derivedFrom":[subQ1,subQ0]});Q65=makeQuery(id+"F0.imprint","IMPRINT",FACE,{"disambiguationData":[TD([[makeQuery(id+"F0.imprint","IMPRINT",EDGE,{"disambiguationData":[TD([[subQ2,-1.0]])],"derivedFrom":subQ1}),1.0]])]});}
            var Q66;
            {var subQ1=sQuery(id+"F0.wireOp",EDGE,"E1.1");var subQ5=sQuery(id+"F0.wireOp",EDGE,"E11.2.0");var subQ8=makeQuery(id+"F0.imprint","INTERSECT",VERTEX,{"derivedFrom":[subQ1,subQ5]});Q66=makeQuery(id+"F0.imprint","IMPRINT",FACE,{"disambiguationData":[TD([[makeQuery(id+"F0.imprint","IMPRINT",EDGE,{"disambiguationData":[TD([[subQ8,-1.0]])],"derivedFrom":subQ1}),1.0]])]});}
            var Q67;
            {var subQ0=sQuery(id+"F0.wireOp",EDGE,"E11.2.0");var subQ1=sQuery(id+"F0.wireOp",EDGE,"E0.1");var subQ2=makeQuery(id+"F0.imprint","INTERSECT",VERTEX,{"derivedFrom":[subQ1,subQ0]});Q67=makeQuery(id+"F0.imprint","IMPRINT",FACE,{"disambiguationData":[TD([[makeQuery(id+"F0.imprint","IMPRINT",EDGE,{"disambiguationData":[TD([[subQ2,1.0]])],"derivedFrom":subQ1}),-1.0]])]});}
            var Q68;
            {var subQ0=sQuery(id+"F0.wireOp",EDGE,"E11.2.0");var subQ1=sQuery(id+"F0.wireOp",EDGE,"E0.1");var subQ2=makeQuery(id+"F0.imprint","INTERSECT",VERTEX,{"derivedFrom":[subQ1,subQ0]});Q68=makeQuery(id+"F0.imprint","IMPRINT",FACE,{"disambiguationData":[TD([[makeQuery(id+"F0.imprint","IMPRINT",EDGE,{"disambiguationData":[TD([[subQ2,-1.0]])],"derivedFrom":subQ1}),-1.0]])]});}
            var Q69;
            {var subQ0=sQuery(id+"F0.wireOp",EDGE,"E11.2.2");var subQ1=sQuery(id+"F0.wireOp",EDGE,"E0.1");var subQ2=makeQuery(id+"F0.imprint","INTERSECT",VERTEX,{"derivedFrom":[subQ1,subQ0]});Q69=makeQuery(id+"F0.imprint","IMPRINT",FACE,{"disambiguationData":[TD([[makeQuery(id+"F0.imprint","IMPRINT",EDGE,{"disambiguationData":[TD([[subQ2,-1.0]])],"derivedFrom":subQ1}),-1.0]])]});}
            var Q70;
            {var subQ0=sQuery(id+"F0.wireOp",EDGE,"E11.2.2");var subQ1=sQuery(id+"F0.wireOp",EDGE,"E1.1");var subQ2=makeQuery(id+"F0.imprint","INTERSECT",VERTEX,{"derivedFrom":[subQ1,subQ0]});Q70=makeQuery(id+"F0.imprint","IMPRINT",FACE,{"disambiguationData":[TD([[makeQuery(id+"F0.imprint","IMPRINT",EDGE,{"disambiguationData":[TD([[subQ2,-1.0]])],"derivedFrom":subQ1}),1.0]])]});}
            var Q71;
            {var subQ0=sQuery(id+"F0.wireOp",EDGE,"E11.2.3");var subQ1=sQuery(id+"F0.wireOp",EDGE,"E0.1");var subQ2=makeQuery(id+"F0.imprint","INTERSECT",VERTEX,{"derivedFrom":[subQ1,subQ0]});Q71=makeQuery(id+"F0.imprint","IMPRINT",FACE,{"disambiguationData":[TD([[makeQuery(id+"F0.imprint","IMPRINT",EDGE,{"disambiguationData":[TD([[subQ2,-1.0]])],"derivedFrom":subQ1}),-1.0]])]});}
            var Q72;
            {var subQ0=sQuery(id+"F0.wireOp",EDGE,"E11.2.3");var subQ1=sQuery(id+"F0.wireOp",EDGE,"E1.1");var subQ2=makeQuery(id+"F0.imprint","INTERSECT",VERTEX,{"derivedFrom":[subQ1,subQ0]});Q72=makeQuery(id+"F0.imprint","IMPRINT",FACE,{"disambiguationData":[TD([[makeQuery(id+"F0.imprint","IMPRINT",EDGE,{"disambiguationData":[TD([[subQ2,-1.0]])],"derivedFrom":subQ1}),1.0]])]});}
            var Q73;
            {var subQ0=sQuery(id+"F0.wireOp",EDGE,"E11.2.4");var subQ1=sQuery(id+"F0.wireOp",EDGE,"E0.1");var subQ2=makeQuery(id+"F0.imprint","INTERSECT",VERTEX,{"derivedFrom":[subQ1,subQ0]});Q73=makeQuery(id+"F0.imprint","IMPRINT",FACE,{"disambiguationData":[TD([[makeQuery(id+"F0.imprint","IMPRINT",EDGE,{"disambiguationData":[TD([[subQ2,-1.0]])],"derivedFrom":subQ1}),-1.0]])]});}
            var Q74;
            {var subQ0=sQuery(id+"F0.wireOp",EDGE,"E11.2.5");var subQ1=sQuery(id+"F0.wireOp",EDGE,"E0.1");var subQ2=makeQuery(id+"F0.imprint","INTERSECT",VERTEX,{"derivedFrom":[subQ1,subQ0]});Q74=makeQuery(id+"F0.imprint","IMPRINT",FACE,{"disambiguationData":[TD([[makeQuery(id+"F0.imprint","IMPRINT",EDGE,{"disambiguationData":[TD([[subQ2,-1.0]])],"derivedFrom":subQ1}),-1.0]])]});}
            var Q75;
            {var subQ4=sQuery(id+"F0.wireOp",EDGE,"E1.1");var subQ6=sQuery(id+"F0.wireOp",EDGE,"E11.2.5");var subQ7=makeQuery(id+"F0.imprint","INTERSECT",VERTEX,{"derivedFrom":[subQ4,subQ6]});Q75=makeQuery(id+"F0.imprint","IMPRINT",FACE,{"disambiguationData":[TD([[makeQuery(id+"F0.imprint","IMPRINT",EDGE,{"disambiguationData":[TD([[subQ7,-1.0]])],"derivedFrom":subQ4}),1.0]])]});}
            var Q76;
            {var subQ0=sQuery(id+"F0.wireOp",EDGE,"E11.2.4");var subQ1=sQuery(id+"F0.wireOp",EDGE,"E1.1");var subQ2=makeQuery(id+"F0.imprint","INTERSECT",VERTEX,{"derivedFrom":[subQ1,subQ0]});Q76=makeQuery(id+"F0.imprint","IMPRINT",FACE,{"disambiguationData":[TD([[makeQuery(id+"F0.imprint","IMPRINT",EDGE,{"disambiguationData":[TD([[subQ2,-1.0]])],"derivedFrom":subQ1}),1.0]])]});}
            var Q77;
            {var subQ0=sQuery(id+"F0.wireOp",EDGE,"E11.2.6");var subQ1=sQuery(id+"F0.wireOp",EDGE,"E0.1");var subQ2=makeQuery(id+"F0.imprint","INTERSECT",VERTEX,{"derivedFrom":[subQ1,subQ0]});Q77=makeQuery(id+"F0.imprint","IMPRINT",FACE,{"disambiguationData":[TD([[makeQuery(id+"F0.imprint","IMPRINT",EDGE,{"disambiguationData":[TD([[subQ2,-1.0]])],"derivedFrom":subQ1}),-1.0]])]});}
            var Q78;
            {var subQ5=sQuery(id+"F0.wireOp",EDGE,"E1.1");var subQ8=sQuery(id+"F0.wireOp",EDGE,"E1.2");var subQ11=makeQuery(id+"F0.imprint","INTERSECT",VERTEX,{"derivedFrom":[subQ5,subQ8]});Q78=makeQuery(id+"F0.imprint","IMPRINT",FACE,{"disambiguationData":[TD([[makeQuery(id+"F0.imprint","IMPRINT",EDGE,{"disambiguationData":[TD([[subQ11,1.0]])],"derivedFrom":subQ5}),1.0]])]});}
            var Q79;
            {var subQ0=sQuery(id+"F0.wireOp",EDGE,"E11.2.6");var subQ1=sQuery(id+"F0.wireOp",EDGE,"E11.1.1");var subQ2=makeQuery(id+"F0.imprint","INTERSECT",VERTEX,{"derivedFrom":[subQ1,subQ0]});Q79=makeQuery(id+"F0.imprint","IMPRINT",FACE,{"disambiguationData":[TD([[makeQuery(id+"F0.imprint","IMPRINT",EDGE,{"disambiguationData":[TD([[subQ2,-1.0]])],"derivedFrom":subQ1}),1.0]])]});}
            var Q80;
            {var subQ4=sQuery(id+"F0.wireOp",EDGE,"E0.1");var subQ7=sQuery(id+"F0.wireOp",EDGE,"E0.2");var subQ9=makeQuery(id+"F0.imprint","INTERSECT",VERTEX,{"derivedFrom":[subQ4,subQ7]});Q80=makeQuery(id+"F0.imprint","IMPRINT",FACE,{"disambiguationData":[TD([[makeQuery(id+"F0.imprint","IMPRINT",EDGE,{"disambiguationData":[TD([[subQ9,1.0]])],"derivedFrom":subQ4}),-1.0]])]});}
            var Q81;
            {var subQ0=sQuery(id+"F0.wireOp",EDGE,"E11.2.7");var subQ1=sQuery(id+"F0.wireOp",EDGE,"E11.1.0");var subQ2=makeQuery(id+"F0.imprint","INTERSECT",VERTEX,{"derivedFrom":[subQ1,subQ0]});Q81=makeQuery(id+"F0.imprint","IMPRINT",FACE,{"disambiguationData":[TD([[makeQuery(id+"F0.imprint","IMPRINT",EDGE,{"disambiguationData":[TD([[subQ2,-1.0]])],"derivedFrom":subQ1}),1.0]])]});}
            var Q82;
            {var subQ0=sQuery(id+"F0.wireOp",EDGE,"E11.1.0");var subQ4=sQuery(id+"F0.wireOp",EDGE,"E1.2");var subQ5=makeQuery(id+"F0.imprint","INTERSECT",VERTEX,{"derivedFrom":[subQ4,subQ0]});Q82=makeQuery(id+"F0.imprint","IMPRINT",FACE,{"disambiguationData":[TD([[makeQuery(id+"F0.imprint","IMPRINT",EDGE,{"disambiguationData":[TD([[subQ5,-1.0]])],"derivedFrom":subQ4}),1.0]])]});}
            var Q83;
            {var subQ0=sQuery(id+"F0.wireOp",EDGE,"E11.1.0");var subQ1=sQuery(id+"F0.wireOp",EDGE,"E0.2");var subQ2=makeQuery(id+"F0.imprint","INTERSECT",VERTEX,{"derivedFrom":[subQ1,subQ0]});Q83=makeQuery(id+"F0.imprint","IMPRINT",FACE,{"disambiguationData":[TD([[makeQuery(id+"F0.imprint","IMPRINT",EDGE,{"disambiguationData":[TD([[subQ2,1.0]])],"derivedFrom":subQ1}),-1.0]])]});}
            var Q84;
            {var subQ0=sQuery(id+"F0.wireOp",EDGE,"E11.1.0");var subQ1=sQuery(id+"F0.wireOp",EDGE,"E0.2");var subQ2=makeQuery(id+"F0.imprint","INTERSECT",VERTEX,{"derivedFrom":[subQ1,subQ0]});Q84=makeQuery(id+"F0.imprint","IMPRINT",FACE,{"disambiguationData":[TD([[makeQuery(id+"F0.imprint","IMPRINT",EDGE,{"disambiguationData":[TD([[subQ2,-1.0]])],"derivedFrom":subQ1}),-1.0]])]});}
            var Q85;
            {var subQ0=sQuery(id+"F0.wireOp",EDGE,"E11.1.2");var subQ1=sQuery(id+"F0.wireOp",EDGE,"E0.2");var subQ2=makeQuery(id+"F0.imprint","INTERSECT",VERTEX,{"derivedFrom":[subQ1,subQ0]});Q85=makeQuery(id+"F0.imprint","IMPRINT",FACE,{"disambiguationData":[TD([[makeQuery(id+"F0.imprint","IMPRINT",EDGE,{"disambiguationData":[TD([[subQ2,-1.0]])],"derivedFrom":subQ1}),-1.0]])]});}
            var Q86;
            {var subQ0=sQuery(id+"F0.wireOp",EDGE,"E11.1.2");var subQ1=sQuery(id+"F0.wireOp",EDGE,"E1.2");var subQ2=makeQuery(id+"F0.imprint","INTERSECT",VERTEX,{"derivedFrom":[subQ1,subQ0]});Q86=makeQuery(id+"F0.imprint","IMPRINT",FACE,{"disambiguationData":[TD([[makeQuery(id+"F0.imprint","IMPRINT",EDGE,{"disambiguationData":[TD([[subQ2,-1.0]])],"derivedFrom":subQ1}),1.0]])]});}
            var Q87;
            {var subQ0=sQuery(id+"F0.wireOp",EDGE,"E11.1.3");var subQ1=sQuery(id+"F0.wireOp",EDGE,"E0.2");var subQ2=makeQuery(id+"F0.imprint","INTERSECT",VERTEX,{"derivedFrom":[subQ1,subQ0]});Q87=makeQuery(id+"F0.imprint","IMPRINT",FACE,{"disambiguationData":[TD([[makeQuery(id+"F0.imprint","IMPRINT",EDGE,{"disambiguationData":[TD([[subQ2,-1.0]])],"derivedFrom":subQ1}),-1.0]])]});}
            var Q88;
            {var subQ0=sQuery(id+"F0.wireOp",EDGE,"E11.1.3");var subQ1=sQuery(id+"F0.wireOp",EDGE,"E1.2");var subQ2=makeQuery(id+"F0.imprint","INTERSECT",VERTEX,{"derivedFrom":[subQ1,subQ0]});Q88=makeQuery(id+"F0.imprint","IMPRINT",FACE,{"disambiguationData":[TD([[makeQuery(id+"F0.imprint","IMPRINT",EDGE,{"disambiguationData":[TD([[subQ2,-1.0]])],"derivedFrom":subQ1}),1.0]])]});}
            var Q89;
            {var subQ0=sQuery(id+"F0.wireOp",EDGE,"E11.1.4");var subQ1=sQuery(id+"F0.wireOp",EDGE,"E0.2");var subQ2=makeQuery(id+"F0.imprint","INTERSECT",VERTEX,{"derivedFrom":[subQ1,subQ0]});Q89=makeQuery(id+"F0.imprint","IMPRINT",FACE,{"disambiguationData":[TD([[makeQuery(id+"F0.imprint","IMPRINT",EDGE,{"disambiguationData":[TD([[subQ2,-1.0]])],"derivedFrom":subQ1}),-1.0]])]});}
            var Q90;
            {var subQ0=sQuery(id+"F0.wireOp",EDGE,"E11.1.4");var subQ1=sQuery(id+"F0.wireOp",EDGE,"E1.2");var subQ2=makeQuery(id+"F0.imprint","INTERSECT",VERTEX,{"derivedFrom":[subQ1,subQ0]});Q90=makeQuery(id+"F0.imprint","IMPRINT",FACE,{"disambiguationData":[TD([[makeQuery(id+"F0.imprint","IMPRINT",EDGE,{"disambiguationData":[TD([[subQ2,-1.0]])],"derivedFrom":subQ1}),1.0]])]});}
            var Q91;
            {var subQ0=sQuery(id+"F0.wireOp",EDGE,"E11.1.3");var subQ1=sQuery(id+"F0.wireOp",EDGE,"E0.2");var subQ2=makeQuery(id+"F0.imprint","INTERSECT",VERTEX,{"derivedFrom":[subQ1,subQ0]});Q91=makeQuery(id+"F0.imprint","IMPRINT",FACE,{"disambiguationData":[TD([[makeQuery(id+"F0.imprint","IMPRINT",EDGE,{"disambiguationData":[TD([[subQ2,-1.0]])],"derivedFrom":subQ1}),-1.0]])]});}
            var Q92;
            {var subQ0=sQuery(id+"F0.wireOp",EDGE,"E11.1.5");var subQ1=sQuery(id+"F0.wireOp",EDGE,"E0.2");var subQ2=makeQuery(id+"F0.imprint","INTERSECT",VERTEX,{"derivedFrom":[subQ1,subQ0]});Q92=makeQuery(id+"F0.imprint","IMPRINT",FACE,{"disambiguationData":[TD([[makeQuery(id+"F0.imprint","IMPRINT",EDGE,{"disambiguationData":[TD([[subQ2,-1.0]])],"derivedFrom":subQ1}),-1.0]])]});}
            var Q93;
            {var subQ0=sQuery(id+"F0.wireOp",EDGE,"E11.1.6");var subQ1=sQuery(id+"F0.wireOp",EDGE,"E0.2");var subQ2=makeQuery(id+"F0.imprint","INTERSECT",VERTEX,{"derivedFrom":[subQ1,subQ0]});Q93=makeQuery(id+"F0.imprint","IMPRINT",FACE,{"disambiguationData":[TD([[makeQuery(id+"F0.imprint","IMPRINT",EDGE,{"disambiguationData":[TD([[subQ2,-1.0]])],"derivedFrom":subQ1}),-1.0]])]});}
            var Q94;
            {var subQ0=sQuery(id+"F0.wireOp",EDGE,"E11.1.6");var subQ1=sQuery(id+"F0.wireOp",EDGE,"E4");var subQ2=makeQuery(id+"F0.imprint","INTERSECT",VERTEX,{"derivedFrom":[subQ1,subQ0]});Q94=makeQuery(id+"F0.imprint","IMPRINT",FACE,{"disambiguationData":[TD([[makeQuery(id+"F0.imprint","IMPRINT",EDGE,{"disambiguationData":[TD([[subQ2,-1.0]])],"derivedFrom":subQ1}),1.0]])]});}
            var Q95;
            {var subQ4=sQuery(id+"F0.wireOp",EDGE,"E1.2");var subQ6=sQuery(id+"F0.wireOp",EDGE,"E11.1.5");var subQ7=makeQuery(id+"F0.imprint","INTERSECT",VERTEX,{"derivedFrom":[subQ4,subQ6]});Q95=makeQuery(id+"F0.imprint","IMPRINT",FACE,{"disambiguationData":[TD([[makeQuery(id+"F0.imprint","IMPRINT",EDGE,{"disambiguationData":[TD([[subQ7,-1.0]])],"derivedFrom":subQ4}),1.0]])]});}
            var Q96;
            {var subQ1=sQuery(id+"F0.wireOp",EDGE,"E0.3");var subQ4=sQuery(id+"F0.wireOp",EDGE,"E0.2");var subQ5=makeQuery(id+"F0.imprint","INTERSECT",VERTEX,{"derivedFrom":[subQ4,subQ1]});Q96=makeQuery(id+"F0.imprint","IMPRINT",FACE,{"disambiguationData":[TD([[makeQuery(id+"F0.imprint","IMPRINT",EDGE,{"disambiguationData":[TD([[subQ5,1.0]])],"derivedFrom":subQ4}),-1.0]])]});}
            var Q97;
            {var subQ9=sQuery(id+"F0.wireOp",EDGE,"E1.0");var subQ29=sQuery(id+"F0.wireOp",EDGE,"E1.5");var subQ42=makeQuery(id+"F0.imprint","INTERSECT",VERTEX,{"derivedFrom":[subQ9,subQ29]});Q97=makeQuery(id+"F0.imprint","IMPRINT",FACE,{"disambiguationData":[TD([[makeQuery(id+"F0.imprint","IMPRINT",EDGE,{"disambiguationData":[TD([[subQ42,-1.0]])],"derivedFrom":subQ9}),-1.0]])]});}
            extrude(context, id + "F1", {"entities" : qUnion([Q0, Q1, Q2, Q3, Q4, Q5, Q6, Q7, Q8, Q9, Q10, Q11, Q12, Q13, Q14, Q15, Q16, Q17, Q18, Q19, Q20, Q21, Q22, Q23, Q24, Q25, Q26, Q27, Q28, Q29, Q30, Q31, Q32, Q33, Q34, Q35, Q36, Q37, Q38, Q39, Q40, Q41, Q42, Q43, Q44, Q45, Q46, Q47, Q48, Q49, Q50, Q51, Q52, Q53, Q54, Q55, Q56, Q57, Q58, Q59, Q60, Q61, Q62, Q63, Q64, Q65, Q66, Q67, Q68, Q69, Q70, Q71, Q72, Q73, Q74, Q75, Q76, Q77, Q78, Q79, Q80, Q81, Q82, Q83, Q84, Q85, Q86, Q87, Q88, Q89, Q90, Q91, Q92, Q93, Q94, Q95, Q96, Q97]), "depth" : 75 * mm});
        }
        {
            var Q0;
            {var subQ1=sQuery(id+"F0.wireOp",EDGE,"E0.0");var subQ6=sQuery(id+"F0.wireOp",EDGE,"E0.5");var subQ7=makeQuery(id+"F0.imprint","INTERSECT",VERTEX,{"derivedFrom":[subQ1,subQ6]});Q0=makeQuery(id+"F0.imprint","IMPRINT",FACE,{"disambiguationData":[TD([[makeQuery(id+"F0.imprint","IMPRINT",EDGE,{"disambiguationData":[TD([[subQ7,-1.0]])],"derivedFrom":subQ1}),-1.0]])]});}
            var Q1;
            {var subQ0=sQuery(id+"F0.wireOp",EDGE,"E11.4.5");var subQ1=sQuery(id+"F0.wireOp",EDGE,"E0.5");var subQ2=makeQuery(id+"F0.imprint","INTERSECT",VERTEX,{"derivedFrom":[subQ1,subQ0]});Q1=makeQuery(id+"F0.imprint","IMPRINT",FACE,{"disambiguationData":[TD([[makeQuery(id+"F0.imprint","IMPRINT",EDGE,{"disambiguationData":[TD([[subQ2,-1.0]])],"derivedFrom":subQ1}),-1.0]])]});}
            var Q2;
            {var subQ0=sQuery(id+"F0.wireOp",EDGE,"E11.4.3");var subQ1=sQuery(id+"F0.wireOp",EDGE,"E0.5");var subQ2=makeQuery(id+"F0.imprint","INTERSECT",VERTEX,{"derivedFrom":[subQ1,subQ0]});Q2=makeQuery(id+"F0.imprint","IMPRINT",FACE,{"disambiguationData":[TD([[makeQuery(id+"F0.imprint","IMPRINT",EDGE,{"disambiguationData":[TD([[subQ2,-1.0]])],"derivedFrom":subQ1}),-1.0]])]});}
            var Q3;
            {var subQ0=sQuery(id+"F0.wireOp",EDGE,"E11.4.0");var subQ1=sQuery(id+"F0.wireOp",EDGE,"E0.5");var subQ2=makeQuery(id+"F0.imprint","INTERSECT",VERTEX,{"derivedFrom":[subQ1,subQ0]});Q3=makeQuery(id+"F0.imprint","IMPRINT",FACE,{"disambiguationData":[TD([[makeQuery(id+"F0.imprint","IMPRINT",EDGE,{"disambiguationData":[TD([[subQ2,-1.0]])],"derivedFrom":subQ1}),-1.0]])]});}
            var Q4;
            {var subQ1=sQuery(id+"F0.wireOp",EDGE,"E0.5");var subQ6=sQuery(id+"F0.wireOp",EDGE,"E0.4");var subQ7=makeQuery(id+"F0.imprint","INTERSECT",VERTEX,{"derivedFrom":[subQ6,subQ1]});Q4=makeQuery(id+"F0.imprint","IMPRINT",FACE,{"disambiguationData":[TD([[makeQuery(id+"F0.imprint","IMPRINT",EDGE,{"disambiguationData":[TD([[subQ7,1.0]])],"derivedFrom":subQ6}),-1.0]])]});}
            var Q5;
            {var subQ0=sQuery(id+"F0.wireOp",EDGE,"E11.5.5");var subQ1=sQuery(id+"F0.wireOp",EDGE,"E0.4");var subQ2=makeQuery(id+"F0.imprint","INTERSECT",VERTEX,{"derivedFrom":[subQ1,subQ0]});Q5=makeQuery(id+"F0.imprint","IMPRINT",FACE,{"disambiguationData":[TD([[makeQuery(id+"F0.imprint","IMPRINT",EDGE,{"disambiguationData":[TD([[subQ2,-1.0]])],"derivedFrom":subQ1}),-1.0]])]});}
            var Q6;
            {var subQ0=sQuery(id+"F0.wireOp",EDGE,"E11.5.3");var subQ1=sQuery(id+"F0.wireOp",EDGE,"E0.4");var subQ2=makeQuery(id+"F0.imprint","INTERSECT",VERTEX,{"derivedFrom":[subQ1,subQ0]});Q6=makeQuery(id+"F0.imprint","IMPRINT",FACE,{"disambiguationData":[TD([[makeQuery(id+"F0.imprint","IMPRINT",EDGE,{"disambiguationData":[TD([[subQ2,-1.0]])],"derivedFrom":subQ1}),-1.0]])]});}
            var Q7;
            {var subQ0=sQuery(id+"F0.wireOp",EDGE,"E11.5.0");var subQ1=sQuery(id+"F0.wireOp",EDGE,"E0.4");var subQ2=makeQuery(id+"F0.imprint","INTERSECT",VERTEX,{"derivedFrom":[subQ1,subQ0]});Q7=makeQuery(id+"F0.imprint","IMPRINT",FACE,{"disambiguationData":[TD([[makeQuery(id+"F0.imprint","IMPRINT",EDGE,{"disambiguationData":[TD([[subQ2,-1.0]])],"derivedFrom":subQ1}),-1.0]])]});}
            var Q8;
            {var subQ1=sQuery(id+"F0.wireOp",EDGE,"E0.3");var subQ6=sQuery(id+"F0.wireOp",EDGE,"E0.4");var subQ7=makeQuery(id+"F0.imprint","INTERSECT",VERTEX,{"derivedFrom":[subQ1,subQ6]});Q8=makeQuery(id+"F0.imprint","IMPRINT",FACE,{"disambiguationData":[TD([[makeQuery(id+"F0.imprint","IMPRINT",EDGE,{"disambiguationData":[TD([[subQ7,1.0]])],"derivedFrom":subQ1}),-1.0]])]});}
            var Q9;
            {var subQ0=sQuery(id+"F0.wireOp",EDGE,"E7.MirrorCS");var subQ1=sQuery(id+"F0.wireOp",EDGE,"E0.3");var subQ2=makeQuery(id+"F0.imprint","INTERSECT",VERTEX,{"derivedFrom":[subQ1,subQ0]});Q9=makeQuery(id+"F0.imprint","IMPRINT",FACE,{"disambiguationData":[TD([[makeQuery(id+"F0.imprint","IMPRINT",EDGE,{"disambiguationData":[TD([[subQ2,-1.0]])],"derivedFrom":subQ1}),-1.0]])]});}
            var Q10;
            {var subQ0=sQuery(id+"F0.wireOp",EDGE,"E5");var subQ1=sQuery(id+"F0.wireOp",EDGE,"E0.3");var subQ2=makeQuery(id+"F0.imprint","INTERSECT",VERTEX,{"derivedFrom":[subQ1,subQ0]});Q10=makeQuery(id+"F0.imprint","IMPRINT",FACE,{"disambiguationData":[TD([[makeQuery(id+"F0.imprint","IMPRINT",EDGE,{"disambiguationData":[TD([[subQ2,-1.0]])],"derivedFrom":subQ1}),-1.0]])]});}
            var Q11;
            {var subQ0=sQuery(id+"F0.wireOp",EDGE,"E2");var subQ1=sQuery(id+"F0.wireOp",EDGE,"E0.3");var subQ2=makeQuery(id+"F0.imprint","INTERSECT",VERTEX,{"derivedFrom":[subQ1,subQ0]});Q11=makeQuery(id+"F0.imprint","IMPRINT",FACE,{"disambiguationData":[TD([[makeQuery(id+"F0.imprint","IMPRINT",EDGE,{"disambiguationData":[TD([[subQ2,1.0]])],"derivedFrom":subQ1}),-1.0]])]});}
            var Q12;
            {var subQ1=sQuery(id+"F0.wireOp",EDGE,"E0.3");var subQ4=sQuery(id+"F0.wireOp",EDGE,"E0.2");var subQ5=makeQuery(id+"F0.imprint","INTERSECT",VERTEX,{"derivedFrom":[subQ4,subQ1]});Q12=makeQuery(id+"F0.imprint","IMPRINT",FACE,{"disambiguationData":[TD([[makeQuery(id+"F0.imprint","IMPRINT",EDGE,{"disambiguationData":[TD([[subQ5,1.0]])],"derivedFrom":subQ4}),-1.0]])]});}
            var Q13;
            {var subQ0=sQuery(id+"F0.wireOp",EDGE,"E11.1.5");var subQ1=sQuery(id+"F0.wireOp",EDGE,"E0.2");var subQ2=makeQuery(id+"F0.imprint","INTERSECT",VERTEX,{"derivedFrom":[subQ1,subQ0]});Q13=makeQuery(id+"F0.imprint","IMPRINT",FACE,{"disambiguationData":[TD([[makeQuery(id+"F0.imprint","IMPRINT",EDGE,{"disambiguationData":[TD([[subQ2,-1.0]])],"derivedFrom":subQ1}),-1.0]])]});}
            var Q14;
            {var subQ0=sQuery(id+"F0.wireOp",EDGE,"E11.1.3");var subQ1=sQuery(id+"F0.wireOp",EDGE,"E0.2");var subQ2=makeQuery(id+"F0.imprint","INTERSECT",VERTEX,{"derivedFrom":[subQ1,subQ0]});Q14=makeQuery(id+"F0.imprint","IMPRINT",FACE,{"disambiguationData":[TD([[makeQuery(id+"F0.imprint","IMPRINT",EDGE,{"disambiguationData":[TD([[subQ2,-1.0]])],"derivedFrom":subQ1}),-1.0]])]});}
            var Q15;
            {var subQ0=sQuery(id+"F0.wireOp",EDGE,"E11.1.0");var subQ1=sQuery(id+"F0.wireOp",EDGE,"E0.2");var subQ2=makeQuery(id+"F0.imprint","INTERSECT",VERTEX,{"derivedFrom":[subQ1,subQ0]});Q15=makeQuery(id+"F0.imprint","IMPRINT",FACE,{"disambiguationData":[TD([[makeQuery(id+"F0.imprint","IMPRINT",EDGE,{"disambiguationData":[TD([[subQ2,-1.0]])],"derivedFrom":subQ1}),-1.0]])]});}
            var Q16;
            {var subQ4=sQuery(id+"F0.wireOp",EDGE,"E0.1");var subQ7=sQuery(id+"F0.wireOp",EDGE,"E0.2");var subQ9=makeQuery(id+"F0.imprint","INTERSECT",VERTEX,{"derivedFrom":[subQ4,subQ7]});Q16=makeQuery(id+"F0.imprint","IMPRINT",FACE,{"disambiguationData":[TD([[makeQuery(id+"F0.imprint","IMPRINT",EDGE,{"disambiguationData":[TD([[subQ9,1.0]])],"derivedFrom":subQ4}),-1.0]])]});}
            var Q17;
            {var subQ0=sQuery(id+"F0.wireOp",EDGE,"E11.2.5");var subQ1=sQuery(id+"F0.wireOp",EDGE,"E0.1");var subQ2=makeQuery(id+"F0.imprint","INTERSECT",VERTEX,{"derivedFrom":[subQ1,subQ0]});Q17=makeQuery(id+"F0.imprint","IMPRINT",FACE,{"disambiguationData":[TD([[makeQuery(id+"F0.imprint","IMPRINT",EDGE,{"disambiguationData":[TD([[subQ2,-1.0]])],"derivedFrom":subQ1}),-1.0]])]});}
            var Q18;
            {var subQ0=sQuery(id+"F0.wireOp",EDGE,"E11.2.3");var subQ1=sQuery(id+"F0.wireOp",EDGE,"E0.1");var subQ2=makeQuery(id+"F0.imprint","INTERSECT",VERTEX,{"derivedFrom":[subQ1,subQ0]});Q18=makeQuery(id+"F0.imprint","IMPRINT",FACE,{"disambiguationData":[TD([[makeQuery(id+"F0.imprint","IMPRINT",EDGE,{"disambiguationData":[TD([[subQ2,-1.0]])],"derivedFrom":subQ1}),-1.0]])]});}
            var Q19;
            {var subQ0=sQuery(id+"F0.wireOp",EDGE,"E11.2.0");var subQ1=sQuery(id+"F0.wireOp",EDGE,"E0.1");var subQ2=makeQuery(id+"F0.imprint","INTERSECT",VERTEX,{"derivedFrom":[subQ1,subQ0]});Q19=makeQuery(id+"F0.imprint","IMPRINT",FACE,{"disambiguationData":[TD([[makeQuery(id+"F0.imprint","IMPRINT",EDGE,{"disambiguationData":[TD([[subQ2,-1.0]])],"derivedFrom":subQ1}),-1.0]])]});}
            var Q20;
            {var subQ4=sQuery(id+"F0.wireOp",EDGE,"E0.1");var subQ6=sQuery(id+"F0.wireOp",EDGE,"E0.0");var subQ7=makeQuery(id+"F0.imprint","INTERSECT",VERTEX,{"derivedFrom":[subQ6,subQ4]});Q20=makeQuery(id+"F0.imprint","IMPRINT",FACE,{"disambiguationData":[TD([[makeQuery(id+"F0.imprint","IMPRINT",EDGE,{"disambiguationData":[TD([[subQ7,1.0]])],"derivedFrom":subQ6}),-1.0]])]});}
            var Q21;
            {var subQ0=sQuery(id+"F0.wireOp",EDGE,"E11.3.5");var subQ1=sQuery(id+"F0.wireOp",EDGE,"E0.0");var subQ2=makeQuery(id+"F0.imprint","INTERSECT",VERTEX,{"derivedFrom":[subQ1,subQ0]});Q21=makeQuery(id+"F0.imprint","IMPRINT",FACE,{"disambiguationData":[TD([[makeQuery(id+"F0.imprint","IMPRINT",EDGE,{"disambiguationData":[TD([[subQ2,-1.0]])],"derivedFrom":subQ1}),-1.0]])]});}
            var Q22;
            {var subQ0=sQuery(id+"F0.wireOp",EDGE,"E11.3.3");var subQ1=sQuery(id+"F0.wireOp",EDGE,"E0.0");var subQ2=makeQuery(id+"F0.imprint","INTERSECT",VERTEX,{"derivedFrom":[subQ1,subQ0]});Q22=makeQuery(id+"F0.imprint","IMPRINT",FACE,{"disambiguationData":[TD([[makeQuery(id+"F0.imprint","IMPRINT",EDGE,{"disambiguationData":[TD([[subQ2,-1.0]])],"derivedFrom":subQ1}),-1.0]])]});}
            var Q23;
            {var subQ0=sQuery(id+"F0.wireOp",EDGE,"E11.3.0");var subQ1=sQuery(id+"F0.wireOp",EDGE,"E0.0");var subQ2=makeQuery(id+"F0.imprint","INTERSECT",VERTEX,{"derivedFrom":[subQ1,subQ0]});Q23=makeQuery(id+"F0.imprint","IMPRINT",FACE,{"disambiguationData":[TD([[makeQuery(id+"F0.imprint","IMPRINT",EDGE,{"disambiguationData":[TD([[subQ2,-1.0]])],"derivedFrom":subQ1}),-1.0]])]});}
            extrude(context, id + "F2", {"entities" : qUnion([Q0, Q1, Q2, Q3, Q4, Q5, Q6, Q7, Q8, Q9, Q10, Q11, Q12, Q13, Q14, Q15, Q16, Q17, Q18, Q19, Q20, Q21, Q22, Q23]), "operationType" : NewBodyOperationType.REMOVE, "depth" : 65 * mm});
        }
        {
            var Q0;
            {var subQ0=sQuery(id+"F0.wireOp",EDGE,"E0.4");Q0=makeQuery(id+"F2.boolean.opBoolean","SPLIT",EDGE,{"disambiguationData":[TD([makeQuery(id+"F2.opExtrude","SWEPT_FACE",FACE,{"disambiguationData":[OSD([sQuery(id+"F0.wireOp",EDGE,"E11.5.6")])]})])],"derivedFrom":makeQuery(id+"F1.opExtrude","CAP_EDGE",EDGE,{"disambiguationData":[OSD([subQ0])],"isStart":true})});}
            var Q1;
            {var subQ0=sQuery(id+"F0.wireOp",EDGE,"E0.4");Q1=makeQuery(id+"F2.boolean.opBoolean","SPLIT",EDGE,{"disambiguationData":[TD([makeQuery(id+"F2.opExtrude","SWEPT_FACE",FACE,{"disambiguationData":[OSD([sQuery(id+"F0.wireOp",EDGE,"E11.5.4")])]})])],"derivedFrom":makeQuery(id+"F1.opExtrude","CAP_EDGE",EDGE,{"disambiguationData":[OSD([subQ0])],"isStart":true})});}
            var Q2;
            {var subQ0=sQuery(id+"F0.wireOp",EDGE,"E0.4");Q2=makeQuery(id+"F2.boolean.opBoolean","SPLIT",EDGE,{"disambiguationData":[TD([makeQuery(id+"F2.opExtrude","SWEPT_FACE",FACE,{"disambiguationData":[OSD([sQuery(id+"F0.wireOp",EDGE,"E11.5.2")])]})])],"derivedFrom":makeQuery(id+"F1.opExtrude","CAP_EDGE",EDGE,{"disambiguationData":[OSD([subQ0])],"isStart":true})});}
            var Q3;
            {var subQ0=sQuery(id+"F0.wireOp",EDGE,"E0.4");Q3=makeQuery(id+"F2.boolean.opBoolean","SPLIT",EDGE,{"disambiguationData":[TD([makeQuery(id+"F2.opExtrude","SWEPT_FACE",FACE,{"disambiguationData":[OSD([sQuery(id+"F0.wireOp",EDGE,"E11.5.0")])]})])],"derivedFrom":makeQuery(id+"F1.opExtrude","CAP_EDGE",EDGE,{"disambiguationData":[OSD([subQ0])],"isStart":true})});}
            var Q4;
            {var subQ0=sQuery(id+"F0.wireOp",EDGE,"E0.3");Q4=makeQuery(id+"F2.boolean.opBoolean","SPLIT",EDGE,{"disambiguationData":[TD([makeQuery(id+"F2.opExtrude","SWEPT_FACE",FACE,{"disambiguationData":[OSD([sQuery(id+"F0.wireOp",EDGE,"E8.MirrorCS")])]})])],"derivedFrom":makeQuery(id+"F1.opExtrude","CAP_EDGE",EDGE,{"disambiguationData":[OSD([subQ0])],"isStart":true})});}
            var Q5;
            {var subQ0=sQuery(id+"F0.wireOp",EDGE,"E0.3");Q5=makeQuery(id+"F2.boolean.opBoolean","SPLIT",EDGE,{"disambiguationData":[TD([makeQuery(id+"F2.opExtrude","SWEPT_FACE",FACE,{"disambiguationData":[OSD([sQuery(id+"F0.wireOp",EDGE,"E6.MirrorCS")])]})])],"derivedFrom":makeQuery(id+"F1.opExtrude","CAP_EDGE",EDGE,{"disambiguationData":[OSD([subQ0])],"isStart":true})});}
            var Q6;
            {var subQ0=sQuery(id+"F0.wireOp",EDGE,"E0.3");Q6=makeQuery(id+"F2.boolean.opBoolean","SPLIT",EDGE,{"disambiguationData":[TD([makeQuery(id+"F2.opExtrude","SWEPT_FACE",FACE,{"disambiguationData":[OSD([sQuery(id+"F0.wireOp",EDGE,"E2")])]})])],"derivedFrom":makeQuery(id+"F1.opExtrude","CAP_EDGE",EDGE,{"disambiguationData":[OSD([subQ0])],"isStart":true})});}
            var Q7;
            {var subQ0=sQuery(id+"F0.wireOp",EDGE,"E0.3");Q7=makeQuery(id+"F2.boolean.opBoolean","SPLIT",EDGE,{"disambiguationData":[TD([makeQuery(id+"F2.opExtrude","SWEPT_FACE",FACE,{"disambiguationData":[OSD([sQuery(id+"F0.wireOp",EDGE,"E3")])]})])],"derivedFrom":makeQuery(id+"F1.opExtrude","CAP_EDGE",EDGE,{"disambiguationData":[OSD([subQ0])],"isStart":true})});}
            var Q8;
            {var subQ0=sQuery(id+"F0.wireOp",EDGE,"E0.2");Q8=makeQuery(id+"F2.boolean.opBoolean","SPLIT",EDGE,{"disambiguationData":[TD([makeQuery(id+"F2.opExtrude","SWEPT_FACE",FACE,{"disambiguationData":[OSD([sQuery(id+"F0.wireOp",EDGE,"E11.1.6")])]})])],"derivedFrom":makeQuery(id+"F1.opExtrude","CAP_EDGE",EDGE,{"disambiguationData":[OSD([subQ0])],"isStart":true})});}
            var Q9;
            {var subQ0=sQuery(id+"F0.wireOp",EDGE,"E0.2");Q9=makeQuery(id+"F2.boolean.opBoolean","SPLIT",EDGE,{"disambiguationData":[TD([makeQuery(id+"F2.opExtrude","SWEPT_FACE",FACE,{"disambiguationData":[OSD([sQuery(id+"F0.wireOp",EDGE,"E11.1.4")])]})])],"derivedFrom":makeQuery(id+"F1.opExtrude","CAP_EDGE",EDGE,{"disambiguationData":[OSD([subQ0])],"isStart":true})});}
            var Q10;
            {var subQ0=sQuery(id+"F0.wireOp",EDGE,"E0.2");Q10=makeQuery(id+"F2.boolean.opBoolean","SPLIT",EDGE,{"disambiguationData":[TD([makeQuery(id+"F2.opExtrude","SWEPT_FACE",FACE,{"disambiguationData":[OSD([sQuery(id+"F0.wireOp",EDGE,"E11.1.2")])]})])],"derivedFrom":makeQuery(id+"F1.opExtrude","CAP_EDGE",EDGE,{"disambiguationData":[OSD([subQ0])],"isStart":true})});}
            var Q11;
            {var subQ0=sQuery(id+"F0.wireOp",EDGE,"E0.2");Q11=makeQuery(id+"F2.boolean.opBoolean","SPLIT",EDGE,{"disambiguationData":[TD([makeQuery(id+"F2.opExtrude","SWEPT_FACE",FACE,{"disambiguationData":[OSD([sQuery(id+"F0.wireOp",EDGE,"E11.1.0")])]})])],"derivedFrom":makeQuery(id+"F1.opExtrude","CAP_EDGE",EDGE,{"disambiguationData":[OSD([subQ0])],"isStart":true})});}
            var Q12;
            {var subQ0=sQuery(id+"F0.wireOp",EDGE,"E0.1");Q12=makeQuery(id+"F2.boolean.opBoolean","SPLIT",EDGE,{"disambiguationData":[TD([makeQuery(id+"F2.opExtrude","SWEPT_FACE",FACE,{"disambiguationData":[OSD([sQuery(id+"F0.wireOp",EDGE,"E11.2.6")])]})])],"derivedFrom":makeQuery(id+"F1.opExtrude","CAP_EDGE",EDGE,{"disambiguationData":[OSD([subQ0])],"isStart":true})});}
            var Q13;
            {var subQ0=sQuery(id+"F0.wireOp",EDGE,"E0.1");Q13=makeQuery(id+"F2.boolean.opBoolean","SPLIT",EDGE,{"disambiguationData":[TD([makeQuery(id+"F2.opExtrude","SWEPT_FACE",FACE,{"disambiguationData":[OSD([sQuery(id+"F0.wireOp",EDGE,"E11.2.4")])]})])],"derivedFrom":makeQuery(id+"F1.opExtrude","CAP_EDGE",EDGE,{"disambiguationData":[OSD([subQ0])],"isStart":true})});}
            var Q14;
            {var subQ0=sQuery(id+"F0.wireOp",EDGE,"E0.1");Q14=makeQuery(id+"F2.boolean.opBoolean","SPLIT",EDGE,{"disambiguationData":[TD([makeQuery(id+"F2.opExtrude","SWEPT_FACE",FACE,{"disambiguationData":[OSD([sQuery(id+"F0.wireOp",EDGE,"E11.2.2")])]})])],"derivedFrom":makeQuery(id+"F1.opExtrude","CAP_EDGE",EDGE,{"disambiguationData":[OSD([subQ0])],"isStart":true})});}
            var Q15;
            {var subQ0=sQuery(id+"F0.wireOp",EDGE,"E0.1");Q15=makeQuery(id+"F2.boolean.opBoolean","SPLIT",EDGE,{"disambiguationData":[TD([makeQuery(id+"F2.opExtrude","SWEPT_FACE",FACE,{"disambiguationData":[OSD([sQuery(id+"F0.wireOp",EDGE,"E11.2.0")])]})])],"derivedFrom":makeQuery(id+"F1.opExtrude","CAP_EDGE",EDGE,{"disambiguationData":[OSD([subQ0])],"isStart":true})});}
            var Q16;
            {var subQ0=sQuery(id+"F0.wireOp",EDGE,"E0.0");Q16=makeQuery(id+"F2.boolean.opBoolean","SPLIT",EDGE,{"disambiguationData":[TD([makeQuery(id+"F2.opExtrude","SWEPT_FACE",FACE,{"disambiguationData":[OSD([sQuery(id+"F0.wireOp",EDGE,"E11.3.6")])]})])],"derivedFrom":makeQuery(id+"F1.opExtrude","CAP_EDGE",EDGE,{"disambiguationData":[OSD([subQ0])],"isStart":true})});}
            var Q17;
            {var subQ0=sQuery(id+"F0.wireOp",EDGE,"E0.0");Q17=makeQuery(id+"F2.boolean.opBoolean","SPLIT",EDGE,{"disambiguationData":[TD([makeQuery(id+"F2.opExtrude","SWEPT_FACE",FACE,{"disambiguationData":[OSD([sQuery(id+"F0.wireOp",EDGE,"E11.3.4")])]})])],"derivedFrom":makeQuery(id+"F1.opExtrude","CAP_EDGE",EDGE,{"disambiguationData":[OSD([subQ0])],"isStart":true})});}
            var Q18;
            {var subQ0=sQuery(id+"F0.wireOp",EDGE,"E0.0");Q18=makeQuery(id+"F2.boolean.opBoolean","SPLIT",EDGE,{"disambiguationData":[TD([makeQuery(id+"F2.opExtrude","SWEPT_FACE",FACE,{"disambiguationData":[OSD([sQuery(id+"F0.wireOp",EDGE,"E11.3.2")])]})])],"derivedFrom":makeQuery(id+"F1.opExtrude","CAP_EDGE",EDGE,{"disambiguationData":[OSD([subQ0])],"isStart":true})});}
            var Q19;
            {var subQ0=sQuery(id+"F0.wireOp",EDGE,"E0.0");Q19=makeQuery(id+"F2.boolean.opBoolean","SPLIT",EDGE,{"disambiguationData":[TD([makeQuery(id+"F2.opExtrude","SWEPT_FACE",FACE,{"disambiguationData":[OSD([sQuery(id+"F0.wireOp",EDGE,"E11.3.0")])]})])],"derivedFrom":makeQuery(id+"F1.opExtrude","CAP_EDGE",EDGE,{"disambiguationData":[OSD([subQ0])],"isStart":true})});}
            var Q20;
            {var subQ0=sQuery(id+"F0.wireOp",EDGE,"E0.5");Q20=makeQuery(id+"F2.boolean.opBoolean","SPLIT",EDGE,{"disambiguationData":[TD([makeQuery(id+"F2.opExtrude","SWEPT_FACE",FACE,{"disambiguationData":[OSD([sQuery(id+"F0.wireOp",EDGE,"E11.4.6")])]})])],"derivedFrom":makeQuery(id+"F1.opExtrude","CAP_EDGE",EDGE,{"disambiguationData":[OSD([subQ0])],"isStart":true})});}
            var Q21;
            {var subQ0=sQuery(id+"F0.wireOp",EDGE,"E0.5");Q21=makeQuery(id+"F2.boolean.opBoolean","SPLIT",EDGE,{"disambiguationData":[TD([makeQuery(id+"F2.opExtrude","SWEPT_FACE",FACE,{"disambiguationData":[OSD([sQuery(id+"F0.wireOp",EDGE,"E11.4.4")])]})])],"derivedFrom":makeQuery(id+"F1.opExtrude","CAP_EDGE",EDGE,{"disambiguationData":[OSD([subQ0])],"isStart":true})});}
            var Q22;
            {var subQ0=sQuery(id+"F0.wireOp",EDGE,"E0.5");Q22=makeQuery(id+"F2.boolean.opBoolean","SPLIT",EDGE,{"disambiguationData":[TD([makeQuery(id+"F2.opExtrude","SWEPT_FACE",FACE,{"disambiguationData":[OSD([sQuery(id+"F0.wireOp",EDGE,"E11.4.2")])]})])],"derivedFrom":makeQuery(id+"F1.opExtrude","CAP_EDGE",EDGE,{"disambiguationData":[OSD([subQ0])],"isStart":true})});}
            var Q23;
            {var subQ0=sQuery(id+"F0.wireOp",EDGE,"E0.5");Q23=makeQuery(id+"F2.boolean.opBoolean","SPLIT",EDGE,{"disambiguationData":[TD([makeQuery(id+"F2.opExtrude","SWEPT_FACE",FACE,{"disambiguationData":[OSD([sQuery(id+"F0.wireOp",EDGE,"E11.4.0")])]})])],"derivedFrom":makeQuery(id+"F1.opExtrude","CAP_EDGE",EDGE,{"disambiguationData":[OSD([subQ0])],"isStart":true})});}
            fillet(context, id + "F3", {"entities" : qUnion([Q0, Q1, Q2, Q3, Q4, Q5, Q6, Q7, Q8, Q9, Q10, Q11, Q12, Q13, Q14, Q15, Q16, Q17, Q18, Q19, Q20, Q21, Q22, Q23]), "radius" : 10 * mm, "tangentPropagation" : true, "allowEdgeOverflow" : false});
        }
        {
            var Q0;
            Q0=makeQuery(id+"F1.opExtrude","CAP_FACE",FACE,{"disambiguationData":[OSD([sQuery(id+"F0.wireOp",EDGE,"E0.0"),sQuery(id+"F0.wireOp",EDGE,"E0.1"),sQuery(id+"F0.wireOp",EDGE,"E0.2"),sQuery(id+"F0.wireOp",EDGE,"E0.3"),sQuery(id+"F0.wireOp",EDGE,"E0.4"),sQuery(id+"F0.wireOp",EDGE,"E0.5")])],"isStart":false});
            var sketch = newSketch(context, id + "F4", { "sketchPlane" : qUnion([Q0])});
            skCircle(sketch, "E12.cCircle", {"center": v(0, 0) * mm, "radius": 37.5 * mm, "construction": true});
            skLineSegment(sketch, "E12.0", {"start": v(21.65, -37.5) * mm, "end": v(-21.65, -37.5) * mm});
            skLineSegment(sketch, "E12.1", {"start": v(-21.65, -37.5) * mm, "end": v(-43.3, 0) * mm});
            skLineSegment(sketch, "E12.2", {"start": v(-43.3, 0) * mm, "end": v(-21.65, 37.5) * mm});
            skLineSegment(sketch, "E12.3", {"start": v(-21.65, 37.5) * mm, "end": v(21.65, 37.5) * mm});
            skLineSegment(sketch, "E12.4", {"start": v(21.65, 37.5) * mm, "end": v(43.3, 0) * mm});
            skLineSegment(sketch, "E12.5", {"start": v(43.3, 0) * mm, "end": v(21.65, -37.5) * mm});
            skPoint(sketch, "E12.0.midPoint", {"position": v(0, -37.5) * mm});
            skSolve(sketch);
        }
        {
            var Q0;
            Q0=makeQuery(id+"F4.imprint","IMPRINT",FACE,{"disambiguationData":[TD([[makeQuery(id+"F4.imprint","IMPRINT",EDGE,{"derivedFrom":sQuery(id+"F4.wireOp",EDGE,"E12.0")}),-1.0]])]});
            extrude(context, id + "F5", {"entities" : qUnion([Q0]), "operationType" : NewBodyOperationType.REMOVE, "oppositeDirection" : true, "depth" : 60 * mm});
        }
        {
            var Q0;
            Q0=makeQuery(id+"F5.boolean.opBoolean","COPY",FACE,{"derivedFrom":makeQuery(id+"F5.opExtrude","SWEPT_FACE",FACE,{"disambiguationData":[OSD([sQuery(id+"F4.wireOp",EDGE,"E12.3")])]})});
            var sketch = newSketch(context, id + "F6", { "sketchPlane" : qUnion([Q0])});
            skCircle(sketch, "E13", {"center": v(0, 35) * mm, "radius": 6 * mm});
            skSolve(sketch);
        }
        {
            var Q0;
            Q0=makeQuery(id+"F6.imprint","IMPRINT",FACE,{"disambiguationData":[TD([[makeQuery(id+"F6.imprint","IMPRINT",EDGE,{"derivedFrom":sQuery(id+"F6.wireOp",EDGE,"E13")}),1.0]])]});
            extrude(context, id + "F7", {"entities" : qUnion([Q0]), "operationType" : NewBodyOperationType.REMOVE, "oppositeDirection" : true, "depth" : 25 * mm});
        }
    });
